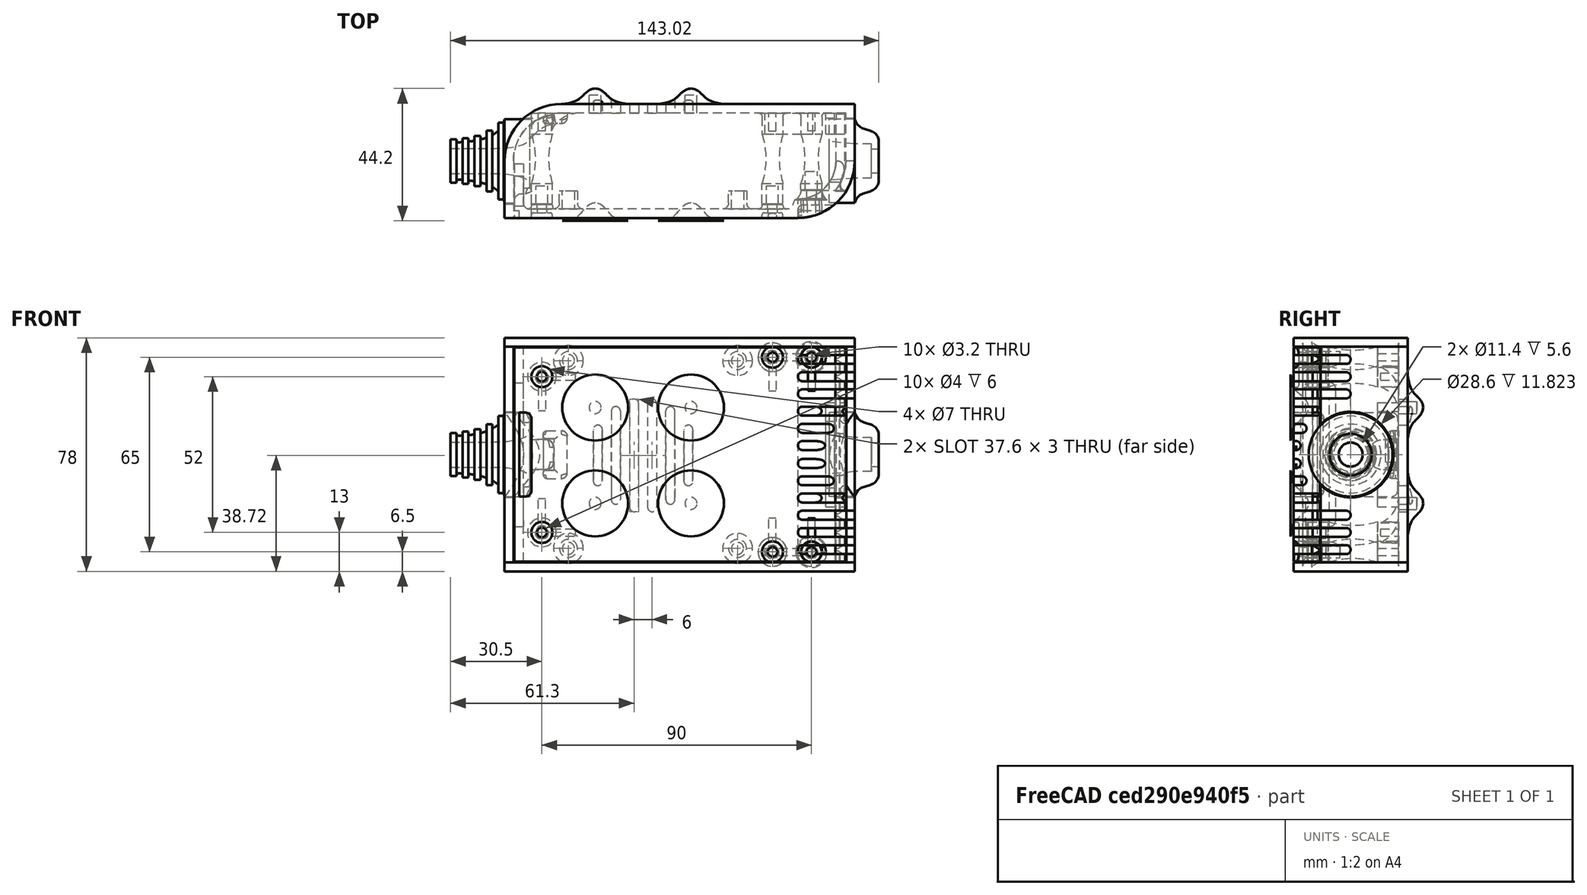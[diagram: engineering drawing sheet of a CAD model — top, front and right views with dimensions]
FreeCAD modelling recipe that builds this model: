
FCSTD DOCUMENT  (FreeCAD 0.19R0.19.2)
Label: enclosure_120
License: All rights reserved
LicenseURL: http://en.wikipedia.org/wiki/All_rights_reserved
objects: Part::Feature×72, Part::Revolution×72, Part::MultiFuse×53, Sketcher::SketchObject×34, Part::Fillet×26, Part::Cut×24, Part::Extrusion×23, Part::Cylinder×22, Part::Box×12, App::MeasureDistance×4
note: 338 computed .brp shape members not serialized (recipe doc carries the construction recipe); baked Part::Feature solids carry a one-line shape summary decoded from their .brp

FEATURE [Sketcher::SketchObject] Sketch  label="topSketch"
  FullyConstrained = true
  sketch-geometry (13):
    g0: LineSegment StartX=117 StartY=19 StartZ=0 EndX=117 EndY=38 EndZ=0
    g1: ArcOfCircle CenterX=98 CenterY=19 CenterZ=0 NormalX=0 NormalY=0 NormalZ=1 AngleXU=0 Radius=19 StartAngle=5.7297 EndAngle=6.28319
    g2: LineSegment StartX=0 StartY=3 StartZ=0 EndX=0 EndY=19 EndZ=0
    g3: LineSegment StartX=19 StartY=38 StartZ=0 EndX=117 EndY=38 EndZ=0
    g4: ArcOfCircle CenterX=19 CenterY=19 CenterZ=0 NormalX=0 NormalY=0 NormalZ=1 AngleXU=0 Radius=19 StartAngle=1.5708 EndAngle=3.14159
    g5: ArcOfCircle CenterX=19 CenterY=19 CenterZ=0 NormalX=0 NormalY=0 NormalZ=1 AngleXU=0 Radius=16 StartAngle=1.5708 EndAngle=3.14159
    g6: ArcOfCircle CenterX=98 CenterY=19 CenterZ=0 NormalX=0 NormalY=0 NormalZ=1 AngleXU=0 Radius=16 StartAngle=5.60905 EndAngle=6.28319
    g7: LineSegment StartX=114 StartY=19 StartZ=0 EndX=114 EndY=35 EndZ=0
    g8: LineSegment StartX=110.5 StartY=9.01251 StartZ=0 EndX=114.163 EndY=9.01251 EndZ=0
    g9: LineSegment StartX=114 StartY=35 StartZ=0 EndX=19 EndY=35 EndZ=0
    g10: LineSegment StartX=0 StartY=3 StartZ=0 EndX=0 EndY=0 EndZ=0
    g11: LineSegment StartX=3 StartY=0 StartZ=0 EndX=0 EndY=0 EndZ=0
    g12: LineSegment StartX=3 StartY=19 StartZ=0 EndX=3 EndY=0 EndZ=0
  constraints (33):
    c: Vertical(g0)
    c: Distance(g0) = 19
    c: Block(g0)
    c: Coincident(g1,g0)
    c: Block(g1)
    c: Vertical(g2)
    c: Block(g2)
    c: Coincident(g3,g0)
    c: Horizontal(g3)
    c: Distance(g3) = 98
    c: Coincident(g4,g3)
    c: Coincident(g4,g2)
    c: Block(g4)
    c: Coincident(g5,g4)
    c: Coincident(g6,g1)
    c: Block(g6)
    c: Block(g5)
    c: Coincident(g7,g6)
    c: Vertical(g7)
    c: Coincident(g8,g6)
    c: Coincident(g8,g1)
    c: Coincident(g9,g7)
    c: Coincident(g9,g5)
    c: Horizontal(g9)
    c: Tangent(g9,g5)
    c: Coincident(g10,g2)
    c: Distance(g10) = 3
    c: Vertical(g10)
    c: Coincident(g11,g10)
    c: Horizontal(g11)
    c: Coincident(g12,g5)
    c: Coincident(g12,g11)
    c: Vertical(g12)
FEATURE [Sketcher::SketchObject] Sketch001  label="bottomSketch"
  FullyConstrained = true
  sketch-geometry (32):
    g0: LineSegment StartX=3.3 StartY=-6.03275e-07 StartZ=0 EndX=98 EndY=-6.03275e-07 EndZ=0
    g1: ArcOfCircle CenterX=98 CenterY=19 CenterZ=0 NormalX=0 NormalY=0 NormalZ=1 AngleXU=0 Radius=19 StartAngle=4.71239 EndAngle=5.71103
    g2: LineSegment StartX=6.3 StartY=8 StartZ=0 EndX=3.3 EndY=8 EndZ=0
    g3: LineSegment StartX=3.3 StartY=8 StartZ=0 EndX=3.3 EndY=-6.03275e-07 EndZ=0
    g4: ArcOfCircle CenterX=8.3 CenterY=5 CenterZ=0 NormalX=0 NormalY=0 NormalZ=1 AngleXU=0 Radius=2 StartAngle=3.14159 EndAngle=4.71239
    g5: LineSegment StartX=6.3 StartY=8 StartZ=0 EndX=6.3 EndY=5 EndZ=0
    g6: ArcOfCircle CenterX=98 CenterY=19 CenterZ=0 NormalX=0 NormalY=0 NormalZ=1 AngleXU=0 Radius=12.7 StartAngle=4.71239 EndAngle=6.28319
    g7: LineSegment StartX=94.7 StartY=3 StartZ=0 EndX=8.3 EndY=3 EndZ=0
    g8-g12: Circle x5 (B-spline internal-alignment scaffolding for g13; pole/knot coordinates omitted)
    g13: BSplineCurve PolesCount=5 KnotsCount=3 Degree=3 IsPeriodic=0
    g14: GeomPoint X=98 Y=6.3 Z=0
    g15: GeomPoint X=96.3938 Y=4.71946 Z=0
    g16: GeomPoint X=94.7 Y=3 Z=0
    g17-g23: Circle x7 (B-spline internal-alignment scaffolding for g24; pole/knot coordinates omitted)
    g24: BSplineCurve PolesCount=7 KnotsCount=5 Degree=3 IsPeriodic=0
    g25-g29: GeomPoint x5 (B-spline internal-alignment scaffolding for g24; pole/knot coordinates omitted)
    g30: ArcOfCircle CenterX=98 CenterY=19 CenterZ=0 NormalX=0 NormalY=0 NormalZ=1 AngleXU=0 Radius=15.7 StartAngle=5.81226 EndAngle=6.28319
    g31: LineSegment StartX=110.7 StartY=19 StartZ=0 EndX=113.7 EndY=19 EndZ=0
  constraints (41):
    c: Horizontal(g0)
    c: Coincident(g1,g0)
    c: Block(g1)
    c: Horizontal(g2)
    c: Distance(g2) = 3
    c: Coincident(g3,g2)
    c: Vertical(g3)
    c: Coincident(g3,g0)
    c: Block(g4)
    c: Block(g2)
    c: Coincident(g5,g2)
    c: Coincident(g5,g4)
    c: Vertical(g5)
    c: Coincident(g6,g1)
    c: Block(g6)
    c: Coincident(g7,g4)
    c: Horizontal(g7)
    c: Block(g0)
    c: Block(g7)
    c: Block(g3)
    c: Coincident(g13,g6)
    c: Weight(g8) = 1
    c: Equal(g8, g9-g12) x4
    c: Coincident(g13,g7)
    c: InternalAlignment(g8-g12 -> g13) x5
    c: InternalAlignment(g14,g13)
    c: InternalAlignment(g15,g13)
    c: InternalAlignment(g16,g13)
    c: Block(g13)
    c: Weight(g17) = 1
    c: Equal(g17, g18-g23) x6
    c: Coincident(g24,g1)
    c: InternalAlignment(g17-g23 -> g24) x7
    c: InternalAlignment(g25-g29 -> g24) x5
    c: Block(g24)
    c: Coincident(g30,g24)
    c: Coincident(g31,g6)
    c: Coincident(g31,g30)
    c: Horizontal(g31)
    c: Block(g31)
    c: Block(g30)
FEATURE [Part::Extrusion] Extrude  label="top"
  Base = -> Sketch
  Dir = (0,0,1)
  DirMode = 2
  FaceMakerClass = Part::FaceMakerBullseye
  LengthFwd = 72
  LengthRev = 0
  Solid = true
  Symmetric = false
FEATURE [Part::Extrusion] Extrude001  label="bottom"
  Base = -> Sketch001
  Dir = (0,0,1)
  DirMode = 2
  FaceMakerClass = Part::FaceMakerBullseye
  LengthFwd = 71.4
  LengthRev = 0
  Placement = pos=(0,0,0.3) rot=(0,0,1;0rad)
  Solid = true
  Symmetric = false
FEATURE [Sketcher::SketchObject] Sketch002  label="topSketch001"
  FullyConstrained = true
  sketch-geometry (6):
    g0: LineSegment StartX=19 StartY=38 StartZ=0 EndX=117 EndY=38 EndZ=0
    g1: ArcOfCircle CenterX=19 CenterY=19 CenterZ=0 NormalX=0 NormalY=0 NormalZ=1 AngleXU=0 Radius=19 StartAngle=1.5708 EndAngle=3.14159
    g2: LineSegment StartX=117 StartY=38 StartZ=0 EndX=117 EndY=19 EndZ=0
    g3: LineSegment StartX=98 StartY=1.0161e-12 StartZ=0 EndX=5.22862e-06 EndY=1.0161e-12 EndZ=0
    g4: LineSegment StartX=5.22862e-06 StartY=19 StartZ=0 EndX=5.22862e-06 EndY=1.0161e-12 EndZ=0
    g5: ArcOfCircle CenterX=98 CenterY=19 CenterZ=0 NormalX=0 NormalY=0 NormalZ=1 AngleXU=0 Radius=19 StartAngle=4.71239 EndAngle=6.28319
  constraints (16):
    c: Horizontal(g0)
    c: Distance(g0) = 98
    c: Coincident(g1,g0)
    c: Block(g1)
    c: Coincident(g2,g0)
    c: Vertical(g2)
    c: Distance(g2) = 19
    c: Horizontal(g3)
    c: Coincident(g4,g1)
    c: Vertical(g4)
    c: Coincident(g3,g4)
    c: Block(g3)
    c: Coincident(g5,g2)
    c: Coincident(g5,g3)
    c: Block(g0)
    c: Block(g5)
FEATURE [Part::Extrusion] Extrude002  label="sideA"
  Base = -> Sketch002
  Dir = (0,0,1)
  DirMode = 2
  FaceMakerClass = Part::FaceMakerBullseye
  LengthFwd = 3
  LengthRev = 0
  Placement = pos=(0,0,-3) rot=(0,0,1;0rad)
  Solid = true
  Symmetric = false
FEATURE [Sketcher::SketchObject] Sketch003  label="topSketch002"
  FullyConstrained = true
  sketch-geometry (6):
    g0: LineSegment StartX=19 StartY=38 StartZ=0 EndX=117 EndY=38 EndZ=0
    g1: ArcOfCircle CenterX=19 CenterY=19 CenterZ=0 NormalX=0 NormalY=0 NormalZ=1 AngleXU=0 Radius=19 StartAngle=1.5708 EndAngle=3.14159
    g2: LineSegment StartX=117 StartY=38 StartZ=0 EndX=117 EndY=19 EndZ=0
    g3: LineSegment StartX=98 StartY=1.0161e-12 StartZ=0 EndX=5.22862e-06 EndY=1.0161e-12 EndZ=0
    g4: LineSegment StartX=5.22862e-06 StartY=19 StartZ=0 EndX=5.22862e-06 EndY=1.0161e-12 EndZ=0
    g5: ArcOfCircle CenterX=98 CenterY=19 CenterZ=0 NormalX=0 NormalY=0 NormalZ=1 AngleXU=0 Radius=19 StartAngle=4.71239 EndAngle=6.28319
  constraints (16):
    c: Horizontal(g0)
    c: Distance(g0) = 98
    c: Coincident(g1,g0)
    c: Block(g1)
    c: Coincident(g2,g0)
    c: Vertical(g2)
    c: Distance(g2) = 19
    c: Horizontal(g3)
    c: Coincident(g4,g1)
    c: Vertical(g4)
    c: Coincident(g3,g4)
    c: Block(g3)
    c: Coincident(g5,g2)
    c: Coincident(g5,g3)
    c: Block(g0)
    c: Block(g5)
FEATURE [Part::Extrusion] Extrude003  label="sideB"
  Base = -> Sketch003
  Dir = (0,0,1)
  DirMode = 2
  FaceMakerClass = Part::FaceMakerBullseye
  LengthFwd = 3
  LengthRev = 0
  Placement = pos=(0,0,72) rot=(0,0,1;0rad)
  Solid = true
  Symmetric = false
FEATURE [Sketcher::SketchObject] Sketch004
  FullyConstrained = true
  MapMode = 3
  Placement = pos=(0,0,0) rot=(1,0,0;1.5708rad)
  Support = -> [Extrude]
  sketch-geometry (8):
    g0: Circle CenterX=80.351 CenterY=-67.6202 CenterZ=0 NormalX=0 NormalY=0 NormalZ=1 AngleXU=0 Radius=2
    g1: Circle CenterX=80.351 CenterY=-67.6202 CenterZ=0 NormalX=0 NormalY=0 NormalZ=1 AngleXU=0 Radius=3
    g2: Circle CenterX=80.351 CenterY=-4.92017 CenterZ=0 NormalX=0 NormalY=0 NormalZ=1 AngleXU=0 Radius=2
    g3: Circle CenterX=80.351 CenterY=-4.92017 CenterZ=0 NormalX=0 NormalY=0 NormalZ=1 AngleXU=0 Radius=3
    g4: Circle CenterX=23.851 CenterY=-4.92017 CenterZ=0 NormalX=0 NormalY=0 NormalZ=1 AngleXU=0 Radius=2
    g5: Circle CenterX=23.851 CenterY=-4.92017 CenterZ=0 NormalX=0 NormalY=0 NormalZ=1 AngleXU=0 Radius=3
    g6: Circle CenterX=23.851 CenterY=-67.6202 CenterZ=0 NormalX=0 NormalY=0 NormalZ=1 AngleXU=0 Radius=2
    g7: Circle CenterX=23.851 CenterY=-67.6202 CenterZ=0 NormalX=0 NormalY=0 NormalZ=1 AngleXU=0 Radius=3
  constraints (8):
    c: Block(g3)
    c: Block(g2)
    c: Block(g1)
    c: Block(g0)
    c: Block(g6)
    c: Block(g7)
    c: Block(g4)
    c: Block(g5)
FEATURE [Part::Extrusion] Extrude004
  Base = -> Sketch004
  Dir = (0,-1,2e-16)
  DirMode = 2
  FaceMakerClass = Part::FaceMakerBullseye
  LengthFwd = 6
  LengthRev = 0
  Placement = pos=(0,9,0) rot=(0,0,1;0rad)
  Solid = true
  Symmetric = false
FEATURE [Sketcher::SketchObject] Sketch005
  FullyConstrained = true
  MapMode = 3
  Placement = pos=(0,0,0) rot=(1,0,0;1.5708rad)
  Support = -> [Extrude]
  sketch-geometry (8):
    g0: Circle CenterX=80.351 CenterY=-67.6202 CenterZ=0 NormalX=0 NormalY=0 NormalZ=1 AngleXU=0 Radius=3
    g1: Circle CenterX=80.351 CenterY=-4.92017 CenterZ=0 NormalX=0 NormalY=0 NormalZ=1 AngleXU=0 Radius=3
    g2: Circle CenterX=23.851 CenterY=-4.92017 CenterZ=0 NormalX=0 NormalY=0 NormalZ=1 AngleXU=0 Radius=3
    g3: Circle CenterX=23.851 CenterY=-67.6202 CenterZ=0 NormalX=0 NormalY=0 NormalZ=1 AngleXU=0 Radius=3
    g4: Circle CenterX=23.851 CenterY=-67.6202 CenterZ=0 NormalX=0 NormalY=0 NormalZ=1 AngleXU=0 Radius=5
    g5: Circle CenterX=80.351 CenterY=-67.6202 CenterZ=0 NormalX=0 NormalY=0 NormalZ=1 AngleXU=0 Radius=5
    g6: Circle CenterX=23.851 CenterY=-4.92017 CenterZ=0 NormalX=0 NormalY=0 NormalZ=1 AngleXU=0 Radius=5
    g7: Circle CenterX=80.351 CenterY=-4.92017 CenterZ=0 NormalX=0 NormalY=0 NormalZ=1 AngleXU=0 Radius=5
  constraints (8):
    c: Block(g1)
    c: Block(g0)
    c: Block(g3)
    c: Block(g2)
    c: Block(g5)
    c: Block(g4)
    c: Block(g6)
    c: Block(g7)
FEATURE [Part::Extrusion] Extrude005
  Base = -> Sketch005
  Dir = (0,-1,2e-16)
  DirMode = 2
  FaceMakerClass = Part::FaceMakerBullseye
  LengthFwd = 2
  LengthRev = 0
  Solid = true
  Symmetric = false
FEATURE [Sketcher::SketchObject] Sketch006
  FullyConstrained = true
  MapMode = 3
  Placement = pos=(0,0,0) rot=(1,0,0;1.5708rad)
  sketch-geometry (8):
    g0: Circle CenterX=80.351 CenterY=-67.6202 CenterZ=0 NormalX=0 NormalY=0 NormalZ=1 AngleXU=0 Radius=3
    g1: Circle CenterX=80.351 CenterY=-4.92017 CenterZ=0 NormalX=0 NormalY=0 NormalZ=1 AngleXU=0 Radius=3
    g2: Circle CenterX=23.851 CenterY=-4.92017 CenterZ=0 NormalX=0 NormalY=0 NormalZ=1 AngleXU=0 Radius=3
    g3: Circle CenterX=23.851 CenterY=-67.6202 CenterZ=0 NormalX=0 NormalY=0 NormalZ=1 AngleXU=0 Radius=3
    g4: Circle CenterX=23.851 CenterY=-67.6202 CenterZ=0 NormalX=0 NormalY=0 NormalZ=1 AngleXU=0 Radius=5
    g5: Circle CenterX=80.351 CenterY=-67.6202 CenterZ=0 NormalX=0 NormalY=0 NormalZ=1 AngleXU=0 Radius=5
    g6: Circle CenterX=23.851 CenterY=-4.92017 CenterZ=0 NormalX=0 NormalY=0 NormalZ=1 AngleXU=0 Radius=5
    g7: Circle CenterX=80.351 CenterY=-4.92017 CenterZ=0 NormalX=0 NormalY=0 NormalZ=1 AngleXU=0 Radius=5
  constraints (8):
    c: Block(g1)
    c: Block(g0)
    c: Block(g3)
    c: Block(g2)
    c: Block(g5)
    c: Block(g4)
    c: Block(g6)
    c: Block(g7)
FEATURE [Part::Extrusion] Extrude007
  Base = -> Sketch006
  Dir = (0,-1,2e-16)
  DirMode = 2
  FaceMakerClass = Part::FaceMakerBullseye
  LengthFwd = 2
  LengthRev = 0
  Solid = true
  Symmetric = false
FEATURE [Part::Fillet] Fillet
  Base = -> Extrude007
  Edges = 4 edges r=1.99: [Edge6,Edge12,Edge18,Edge24]
FEATURE [Part::Cut] Cut
  Base = -> Extrude005
  Placement = pos=(0,5,0) rot=(0,0,1;0rad)
  Tool = -> Fillet
FEATURE [Part::MultiFuse] Fusion  label="pCBScrews"
  Placement = pos=(-2.5,0,72.3) rot=(0,0,1;0rad)
  Shapes = -> [Extrude004,Cut]
FEATURE [App::MeasureDistance] Distance  label="Distance: 0.69 mm"
  Distance = 0.685967
  P1 = (24.0138,2.9647,0.3)
  P2 = (23.8901,3,-0.373787)
FEATURE [App::MeasureDistance] Distance001  label="Distance: 0.53 mm"
  Distance = 0.533607
  P1 = (80.2939,3,72.2334)
  P2 = (80.281,2.99661,71.7)
FEATURE [Part::Fillet] Fillet001
  Base = -> Extrude001
  Edges = 1 edges r=2.4: [Edge17]
FEATURE [Part::Fillet] Fillet002  label="bottom001"
  Base = -> Fillet001
  Edges = 1 edges r=2.4: [Edge36]
FEATURE [Part::Fillet] Fillet003  label="top001"
  Base = -> Extrude
  Edges = 1 edges r=2: [Edge1]
FEATURE [Sketcher::SketchObject] Sketch007
  FullyConstrained = true
  sketch-geometry (16):
    g0: LineSegment StartX=4 StartY=0 StartZ=0 EndX=4 EndY=2.4 EndZ=0
    g1: LineSegment StartX=4 StartY=2.4 StartZ=0 EndX=7 EndY=2.4 EndZ=0
    g2: LineSegment StartX=4 StartY=0 StartZ=0 EndX=5.7 EndY=0 EndZ=0
    g3: LineSegment StartX=5.7 StartY=0 StartZ=0 EndX=5.7 EndY=-5.6 EndZ=0
    g4-g8: Circle x5 (B-spline internal-alignment scaffolding for g9; pole/knot coordinates omitted)
    g9: BSplineCurve PolesCount=5 KnotsCount=3 Degree=3 IsPeriodic=0
    g10: GeomPoint X=7 Y=2.4 Z=0
    g11: GeomPoint X=10.4582 Y=-1.55472 Z=0
    g12: GeomPoint X=14 Y=-5.6 Z=0
    g13: LineSegment StartX=14 StartY=-5.6 StartZ=0 EndX=14 EndY=-14.1 EndZ=0
    g14: LineSegment StartX=14 StartY=-14.1 StartZ=0 EndX=6.5 EndY=-14.1 EndZ=0
    g15: LineSegment StartX=5.7 StartY=-5.6 StartZ=0 EndX=6.5 EndY=-14.1 EndZ=0
  constraints (28):
    c: Distance(g0) = 2.4
    c: Vertical(g0)
    c: Block(g0)
    c: Coincident(g1,g0)
    c: Horizontal(g1)
    c: Distance(g1) = 3
    c: Coincident(g2,g0)
    c: Horizontal(g2)
    c: Distance(g2) = 1.7
    c: Coincident(g3,g2)
    c: Vertical(g3)
    c: Distance(g3) = 5.6
    c: Coincident(g9,g1)
    c: Weight(g4) = 1
    c: Equal(g4, g5-g8) x4
    c: InternalAlignment(g4-g8 -> g9) x5
    c: InternalAlignment(g10,g9)
    c: InternalAlignment(g11,g9)
    c: InternalAlignment(g12,g9)
    c: Block(g9)
    c: Coincident(g13,g9)
    c: Vertical(g13)
    c: Distance(g13) = 8.5
    c: Coincident(g14,g13)
    c: Horizontal(g14)
    c: Distance(g14) = 7.5
    c: Coincident(g15,g3)
    c: Coincident(g15,g14)
FEATURE [Part::Feature] Face
  shape: bbox 10 x 16.5 x 2e-07 mm, 1 faces, 0 solids (baked)
FEATURE [Part::Revolution] Revolve  label="plugHousing"
  Angle = 360
  Axis = (0,1,0)
  Base = (0,0,0)
  FaceMakerClass = Part::FaceMakerBullseye
  Placement = pos=(0,0,36.15) rot=(0,0,1;0rad)
  Solid = false
  Source = -> Face
  Symmetric = false
FEATURE [Part::Feature] Face001
  shape: bbox 10 x 16.5 x 2e-07 mm, 1 faces, 0 solids (baked)
FEATURE [Part::Revolution] Revolve001  label="plugHousing001"
  Angle = 360
  Axis = (0,1,0)
  Base = (0,0,0)
  FaceMakerClass = Part::FaceMakerBullseye
  Placement = pos=(0,0,36.15) rot=(0,0,1;0rad)
  Solid = false
  Source = -> Face001
  Symmetric = false
FEATURE [Part::MultiFuse] Fusion001  label="plugHousing002"
  Placement = pos=(0,0,0) rot=(0,0,1;1.5708rad)
  Shapes = -> [Revolve001,Revolve]
FEATURE [Part::Feature] Face002
  shape: bbox 10 x 16.5 x 2e-07 mm, 1 faces, 0 solids (baked)
FEATURE [Part::Revolution] Revolve003  label="plugHousing005"
  Angle = 360
  Axis = (0,1,0)
  Base = (0,0,0)
  FaceMakerClass = Part::FaceMakerBullseye
  Placement = pos=(0,0,36.15) rot=(0,0,1;0rad)
  Solid = false
  Source = -> Face002
  Symmetric = false
FEATURE [Part::Feature] Face003
  shape: bbox 10 x 16.5 x 2e-07 mm, 1 faces, 0 solids (baked)
FEATURE [Part::Revolution] Revolve002  label="plugHousing003"
  Angle = 360
  Axis = (0,1,0)
  Base = (0,0,0)
  FaceMakerClass = Part::FaceMakerBullseye
  Placement = pos=(0,0,36.15) rot=(0,0,1;0rad)
  Solid = false
  Source = -> Face003
  Symmetric = false
FEATURE [Part::MultiFuse] Fusion002  label="plugHousing004"
  Placement = pos=(0,0,0) rot=(0,0,1;1.5708rad)
  Shapes = -> [Revolve002,Revolve003]
FEATURE [Part::MultiFuse] Fusion003  label="plugHousing006"
  Placement = pos=(0,19,0) rot=(0,0,1;3.14159rad)
  Shapes = -> [Fusion002,Fusion001]
FEATURE [Part::Feature] Face004
  shape: bbox 10 x 16.5 x 2e-07 mm, 1 faces, 0 solids (baked)
FEATURE [Part::Revolution] Revolve006  label="plugHousing010"
  Angle = 360
  Axis = (0,1,0)
  Base = (0,0,0)
  FaceMakerClass = Part::FaceMakerBullseye
  Placement = pos=(0,0,36.15) rot=(0,0,1;0rad)
  Solid = false
  Source = -> Face004
  Symmetric = false
FEATURE [Part::Feature] Face005
  shape: bbox 10 x 16.5 x 2e-07 mm, 1 faces, 0 solids (baked)
FEATURE [Part::Revolution] Revolve007  label="plugHousing011"
  Angle = 360
  Axis = (0,1,0)
  Base = (0,0,0)
  FaceMakerClass = Part::FaceMakerBullseye
  Placement = pos=(0,0,36.15) rot=(0,0,1;0rad)
  Solid = false
  Source = -> Face005
  Symmetric = false
FEATURE [Part::Feature] Face006
  shape: bbox 10 x 16.5 x 2e-07 mm, 1 faces, 0 solids (baked)
FEATURE [Part::Revolution] Revolve004  label="plugHousing007"
  Angle = 360
  Axis = (0,1,0)
  Base = (0,0,0)
  FaceMakerClass = Part::FaceMakerBullseye
  Placement = pos=(0,0,36.15) rot=(0,0,1;0rad)
  Solid = false
  Source = -> Face006
  Symmetric = false
FEATURE [Part::MultiFuse] Fusion004  label="plugHousing009"
  Placement = pos=(0,0,0) rot=(0,0,1;1.5708rad)
  Shapes = -> [Revolve004,Revolve007]
FEATURE [Part::Feature] Face007
  shape: bbox 10 x 16.5 x 2e-07 mm, 1 faces, 0 solids (baked)
FEATURE [Part::Revolution] Revolve005  label="plugHousing008"
  Angle = 360
  Axis = (0,1,0)
  Base = (0,0,0)
  FaceMakerClass = Part::FaceMakerBullseye
  Placement = pos=(0,0,36.15) rot=(0,0,1;0rad)
  Solid = false
  Source = -> Face007
  Symmetric = false
FEATURE [Part::MultiFuse] Fusion005  label="plugHousing012"
  Placement = pos=(0,0,0) rot=(0,0,1;1.5708rad)
  Shapes = -> [Revolve006,Revolve005]
FEATURE [Part::MultiFuse] Fusion006  label="plugHousing013"
  Placement = pos=(0,19,0) rot=(0,0,1;3.14159rad)
  Shapes = -> [Fusion005,Fusion004]
FEATURE [Part::MultiFuse] Fusion007  label="plugHousing014"
  Placement = pos=(122.621,0,-0.15) rot=(0,0,1;0rad)
  Shapes = -> [Fusion003,Fusion006]
FEATURE [Part::Cylinder] Cylinder002
  Angle = 360
  AttacherType = Attacher::AttachEngine3D
  Height = 20
  Placement = pos=(0,0,36.15) rot=(0,0,1;0rad)
  Radius = 4
FEATURE [Part::Cylinder] Cylinder003
  Angle = 360
  AttacherType = Attacher::AttachEngine3D
  Height = 10
  Placement = pos=(0,0,36.15) rot=(0,0,1;0rad)
  Radius = 4
FEATURE [Part::MultiFuse] Fusion009  label="removeToCreateHoleForPlugHousing"
  Placement = pos=(70,19,36.15) rot=(0,1,0;1.5708rad)
  Shapes = -> [Cylinder002,Cylinder003]
FEATURE [Part::Cylinder] Cylinder004
  Angle = 360
  AttacherType = Attacher::AttachEngine3D
  Height = 20
  Placement = pos=(0,0,36.15) rot=(0,0,1;0rad)
  Radius = 4
FEATURE [Part::Cylinder] Cylinder005
  Angle = 360
  AttacherType = Attacher::AttachEngine3D
  Height = 10
  Placement = pos=(0,0,36.15) rot=(0,0,1;0rad)
  Radius = 4
FEATURE [Part::MultiFuse] Fusion010  label="removeToCreateHoleForPlugHousing001"
  Placement = pos=(70,19,36.15) rot=(0,1,0;1.5708rad)
  Shapes = -> [Cylinder004,Cylinder005]
FEATURE [Part::Cut] Cut001
  Base = -> Fillet003
  Tool = -> Fusion010
FEATURE [Part::Cut] Cut002  label="Bottom"
  Base = -> Fillet002
  Tool = -> Fusion009
FEATURE [Part::Feature] Face008
  shape: bbox 10 x 16.5 x 2e-07 mm, 1 faces, 0 solids (baked)
FEATURE [Part::Revolution] Revolve011  label="plugHousing021"
  Angle = 360
  Axis = (0,1,0)
  Base = (0,0,0)
  FaceMakerClass = Part::FaceMakerBullseye
  Placement = pos=(0,0,36.15) rot=(0,0,1;0rad)
  Solid = false
  Source = -> Face008
  Symmetric = false
FEATURE [Part::Feature] Face009
  shape: bbox 10 x 16.5 x 2e-07 mm, 1 faces, 0 solids (baked)
FEATURE [Part::Revolution] Revolve012  label="plugHousing022"
  Angle = 360
  Axis = (0,1,0)
  Base = (0,0,0)
  FaceMakerClass = Part::FaceMakerBullseye
  Placement = pos=(0,0,36.15) rot=(0,0,1;0rad)
  Solid = false
  Source = -> Face009
  Symmetric = false
FEATURE [Part::Feature] Face010 .. Face013  x4 (patterned run collapsed; names and placements below)
  shape: bbox 10 x 16.5 x 2e-07 mm, 1 faces, 0 solids (baked)
FEATURE [Part::Revolution] Revolve015  label="plugHousing027"
  Angle = 360
  Axis = (0,1,0)
  Base = (0,0,0)
  FaceMakerClass = Part::FaceMakerBullseye
  Placement = pos=(0,0,36.15) rot=(0,0,1;0rad)
  Solid = false
  Source = -> Face013
  Symmetric = false
FEATURE [Part::Feature] Face014
  shape: bbox 10 x 16.5 x 2e-07 mm, 1 faces, 0 solids (baked)
FEATURE [Part::Feature] Face015
  shape: bbox 10 x 16.5 x 2e-07 mm, 1 faces, 0 solids (baked)
FEATURE [Part::Feature] Face016
  shape: bbox 10 x 16.5 x 2e-07 mm, 1 faces, 0 solids (baked)
FEATURE [Part::Revolution] Revolve019  label="plugHousing033"
  Angle = 360
  Axis = (0,1,0)
  Base = (0,0,0)
  FaceMakerClass = Part::FaceMakerBullseye
  Placement = pos=(0,0,36.15) rot=(0,0,1;0rad)
  Solid = false
  Source = -> Face016
  Symmetric = false
FEATURE [Part::Feature] Face017
  shape: bbox 10 x 16.5 x 2e-07 mm, 1 faces, 0 solids (baked)
FEATURE [Part::Revolution] Revolve020  label="plugHousing034"
  Angle = 360
  Axis = (0,1,0)
  Base = (0,0,0)
  FaceMakerClass = Part::FaceMakerBullseye
  Placement = pos=(0,0,36.15) rot=(0,0,1;0rad)
  Solid = false
  Source = -> Face017
  Symmetric = false
FEATURE [Part::Feature] Face018
  shape: bbox 10 x 16.5 x 2e-07 mm, 1 faces, 0 solids (baked)
FEATURE [Part::Revolution] Revolve016  label="plugHousing030"
  Angle = 360
  Axis = (0,1,0)
  Base = (0,0,0)
  FaceMakerClass = Part::FaceMakerBullseye
  Placement = pos=(0,0,36.15) rot=(0,0,1;0rad)
  Solid = false
  Source = -> Face018
  Symmetric = false
FEATURE [Part::MultiFuse] Fusion020  label="plugHousing038"
  Placement = pos=(0,0,0) rot=(0,0,1;1.5708rad)
  Shapes = -> [Revolve016,Revolve020]
FEATURE [Part::Feature] Face019
  shape: bbox 10 x 16.5 x 2e-07 mm, 1 faces, 0 solids (baked)
FEATURE [Part::Feature] Face020
  shape: bbox 10 x 16.5 x 2e-07 mm, 1 faces, 0 solids (baked)
FEATURE [Part::Revolution] Revolve017  label="plugHousing031"
  Angle = 360
  Axis = (0,1,0)
  Base = (0,0,0)
  FaceMakerClass = Part::FaceMakerBullseye
  Placement = pos=(0,0,36.15) rot=(0,0,1;0rad)
  Solid = false
  Source = -> Face020
  Symmetric = false
FEATURE [Part::MultiFuse] Fusion021  label="plugHousing039"
  Placement = pos=(0,0,0) rot=(0,0,1;1.5708rad)
  Shapes = -> [Revolve019,Revolve017]
FEATURE [Part::MultiFuse] Fusion023  label="plugHousing041"
  Placement = pos=(0,19,0) rot=(0,0,1;3.14159rad)
  Shapes = -> [Fusion021,Fusion020]
FEATURE [Part::Revolution] Revolve022  label="plugHousing043"
  Angle = 360
  Axis = (0,1,0)
  Base = (0,0,0)
  FaceMakerClass = Part::FaceMakerBullseye
  Placement = pos=(0,0,36.15) rot=(0,0,1;0rad)
  Solid = false
  Source = -> Face019
  Symmetric = false
FEATURE [Part::Feature] Face021
  shape: bbox 10 x 16.5 x 2e-07 mm, 1 faces, 0 solids (baked)
FEATURE [Part::Revolution] Revolve023  label="plugHousing044"
  Angle = 360
  Axis = (0,1,0)
  Base = (0,0,0)
  FaceMakerClass = Part::FaceMakerBullseye
  Placement = pos=(0,0,36.15) rot=(0,0,1;0rad)
  Solid = false
  Source = -> Face021
  Symmetric = false
FEATURE [Part::Feature] Face022
  shape: bbox 10 x 16.5 x 2e-07 mm, 1 faces, 0 solids (baked)
FEATURE [Part::Revolution] Revolve018  label="plugHousing032"
  Angle = 360
  Axis = (0,1,0)
  Base = (0,0,0)
  FaceMakerClass = Part::FaceMakerBullseye
  Placement = pos=(0,0,36.15) rot=(0,0,1;0rad)
  Solid = false
  Source = -> Face022
  Symmetric = false
FEATURE [Part::MultiFuse] Fusion022  label="plugHousing040"
  Placement = pos=(0,0,0) rot=(0,0,1;1.5708rad)
  Shapes = -> [Revolve018,Revolve023]
FEATURE [Part::Feature] Face023
  shape: bbox 10 x 16.5 x 2e-07 mm, 1 faces, 0 solids (baked)
FEATURE [Part::Revolution] Revolve021  label="plugHousing035"
  Angle = 360
  Axis = (0,1,0)
  Base = (0,0,0)
  FaceMakerClass = Part::FaceMakerBullseye
  Placement = pos=(0,0,36.15) rot=(0,0,1;0rad)
  Solid = false
  Source = -> Face023
  Symmetric = false
FEATURE [Part::MultiFuse] Fusion018  label="plugHousing036"
  Placement = pos=(0,0,0) rot=(0,0,1;1.5708rad)
  Shapes = -> [Revolve022,Revolve021]
FEATURE [Part::MultiFuse] Fusion019  label="plugHousing037"
  Placement = pos=(0,19,0) rot=(0,0,1;3.14159rad)
  Shapes = -> [Fusion018,Fusion022]
FEATURE [Part::MultiFuse] Fusion024  label="plugHousing042"
  Placement = pos=(122.621,0,-0.15) rot=(0,0,1;0rad)
  Shapes = -> [Fusion023,Fusion019]
FEATURE [Part::Cylinder] Cylinder006
  Angle = 360
  AttacherType = Attacher::AttachEngine3D
  Height = 20
  Placement = pos=(0,0,36.15) rot=(0,0,1;0rad)
  Radius = 14.3
FEATURE [Part::Cylinder] Cylinder007
  Angle = 360
  AttacherType = Attacher::AttachEngine3D
  Height = 10
  Placement = pos=(0,0,36.15) rot=(0,0,1;0rad)
  Radius = 4
FEATURE [Part::MultiFuse] Fusion026  label="removeToCreteHoleForPlugHousing"
  Placement = pos=(70,19,36) rot=(0,1,0;1.5708rad)
  Shapes = -> [Cylinder006,Cylinder007]
FEATURE [Part::Box] Box001  label="Cube001"
  AttacherType = Attacher::AttachEngine3D
  Height = 28
  Length = 3
  Placement = pos=(110.7,19,22) rot=(0,0,1;0rad)
  Width = 15.7
FEATURE [Part::Cut] Cut003  label="top002"
  Base = -> Cut001
  Tool = -> Fusion007
FEATURE [Part::Revolution] Revolve008  label="plugHousing015"
  Angle = 360
  Axis = (0,1,0)
  Base = (0,0,0)
  FaceMakerClass = Part::FaceMakerBullseye
  Placement = pos=(0,0,36.15) rot=(0,0,1;0rad)
  Solid = false
  Source = -> Face010
  Symmetric = false
FEATURE [Part::MultiFuse] Fusion013  label="plugHousing020"
  Placement = pos=(0,0,0) rot=(0,0,1;1.5708rad)
  Shapes = -> [Revolve008,Revolve012]
FEATURE [Part::Cut] Cut004  label="top003"
  Base = -> Cut003
  Placement = pos=(1,0,0) rot=(0,0,1;0rad)
  Tool = -> Fusion026
FEATURE [Part::Cylinder] Cylinder008
  Angle = 360
  AttacherType = Attacher::AttachEngine3D
  Height = 20
  Placement = pos=(0,0,36.15) rot=(0,0,1;0rad)
  Radius = 10.3
FEATURE [Part::Cylinder] Cylinder009
  Angle = 360
  AttacherType = Attacher::AttachEngine3D
  Height = 10
  Placement = pos=(0,0,36.15) rot=(0,0,1;0rad)
  Radius = 4
FEATURE [Part::MultiFuse] Fusion027  label="removeToCreteHoleForPlugHousing001"
  Placement = pos=(70,19,36) rot=(0,1,0;1.5708rad)
  Shapes = -> [Cylinder008,Cylinder009]
FEATURE [Part::Cut] Cut005  label="plugHousingTab"
  Base = -> Box001
  Tool = -> Fusion027
FEATURE [Part::MultiFuse] Fusion028  label="plugHousing045"
  Shapes = -> [Fusion024,Cut005]
FEATURE [Part::Box] Box002  label="Cube002"
  AttacherType = Attacher::AttachEngine3D
  Height = 28.8
  Length = 3
  Placement = pos=(107.3,28,21.6) rot=(0,0,1;0rad)
  Width = 7
FEATURE [Part::Box] Box003  label="Cube003"
  AttacherType = Attacher::AttachEngine3D
  Height = 3
  Length = 6.4
  Placement = pos=(107.3,28,18.6) rot=(0,0,1;0rad)
  Width = 7
FEATURE [Part::Box] Box004  label="Cube004"
  AttacherType = Attacher::AttachEngine3D
  Height = 3
  Length = 6.4
  Placement = pos=(107.3,28,50.4) rot=(0,0,1;0rad)
  Width = 7
FEATURE [Part::MultiFuse] Fusion029  label="plugHousingBracketHolder"
  Shapes = -> [Box004,Box002,Box003]
FEATURE [Part::Cylinder] Cylinder010
  Angle = 360
  AttacherType = Attacher::AttachEngine3D
  Height = 20
  Placement = pos=(0,0,36.15) rot=(0,0,1;0rad)
  Radius = 14.3
FEATURE [Part::Cylinder] Cylinder011
  Angle = 360
  AttacherType = Attacher::AttachEngine3D
  Height = 10
  Placement = pos=(0,0,36.15) rot=(0,0,1;0rad)
  Radius = 4
FEATURE [Part::MultiFuse] Fusion030  label="removeToCreteHoleForPlugHousing002"
  Placement = pos=(70,19,36) rot=(0,1,0;1.5708rad)
  Shapes = -> [Cylinder010,Cylinder011]
FEATURE [Part::Cut] Cut006  label="plugHousingBracketHolder001"
  Base = -> Fusion029
  Tool = -> Fusion030
FEATURE [Part::Cylinder] Cylinder012
  Angle = 360
  AttacherType = Attacher::AttachEngine3D
  Height = 20
  Placement = pos=(0,0,36.15) rot=(0,0,1;0rad)
  Radius = 7
FEATURE [Part::Cylinder] Cylinder013
  Angle = 360
  AttacherType = Attacher::AttachEngine3D
  Height = 10
  Placement = pos=(0,0,36.15) rot=(0,0,1;0rad)
  Radius = 4
FEATURE [Part::MultiFuse] Fusion032  label="removeToCreteHoleForPlugHousing003"
  Placement = pos=(70,19,36) rot=(0,1,0;1.5708rad)
  Shapes = -> [Cylinder012,Cylinder013]
FEATURE [Part::Cut] Cut007  label="bottom002"
  Base = -> Cut002
  Tool = -> Fusion032
FEATURE [Sketcher::SketchObject] Sketch008
  FullyConstrained = true
  sketch-geometry (54):
    g0: LineSegment StartX=-4.2 StartY=0 StartZ=0 EndX=-6.2 EndY=0 EndZ=0
    g1: LineSegment StartX=-14 StartY=-18 StartZ=0 EndX=-14 EndY=-26.5 EndZ=0
    g2: LineSegment StartX=-4.2 StartY=0 StartZ=0 EndX=-4.2 EndY=-13.4877 EndZ=0
    g3: Circle CenterX=-4.2 CenterY=-13.4877 CenterZ=0 NormalX=0 NormalY=0 NormalZ=1 AngleXU=0 Radius=1
    g4: Circle CenterX=-4.2 CenterY=-26.5 CenterZ=0 NormalX=0 NormalY=0 NormalZ=1 AngleXU=0 Radius=1
    g5: Circle CenterX=-8.2 CenterY=-26.5 CenterZ=0 NormalX=0 NormalY=0 NormalZ=1 AngleXU=0 Radius=1
    g6: BSplineCurve PolesCount=3 KnotsCount=2 Degree=2 IsPeriodic=0
    g7: GeomPoint X=-4.2 Y=-13.4877 Z=0
    g8: GeomPoint X=-8.2 Y=-26.5 Z=0
    g9: LineSegment StartX=-14 StartY=-26.5 StartZ=0 EndX=-8.2 EndY=-26.5 EndZ=0
    g10: LineSegment StartX=-10.15 StartY=-12 StartZ=0 EndX=-10.15 EndY=-14 EndZ=0
    g11: LineSegment StartX=-12.8401 StartY=-16 StartZ=0 EndX=-10.1571 EndY=-16 EndZ=0
    g12: LineSegment StartX=-10.15 StartY=-14 StartZ=0 EndX=-8.70761 EndY=-14 EndZ=0
    g13: LineSegment StartX=-12.8401 StartY=-16 StartZ=0 EndX=-12.8401 EndY=-17.6958 EndZ=0
    g14: LineSegment StartX=-10.15 StartY=-12 StartZ=0 EndX=-7.79258 EndY=-12 EndZ=0
    g15: Circle CenterX=-6.2215 CenterY=-2 CenterZ=0 NormalX=0 NormalY=0 NormalZ=1 AngleXU=0 Radius=1
    g16: Circle CenterX=-6.22762 CenterY=-2.58724 CenterZ=0 NormalX=0 NormalY=0 NormalZ=1 AngleXU=0 Radius=1
    g17: Circle CenterX=-6.32538 CenterY=-4 CenterZ=0 NormalX=0 NormalY=0 NormalZ=1 AngleXU=0 Radius=1
    g18: BSplineCurve PolesCount=3 KnotsCount=2 Degree=2 IsPeriodic=0
    g19: GeomPoint X=-6.2215 Y=-2 Z=0
    g20: GeomPoint X=-6.32538 Y=-4 Z=0
    g21: Circle CenterX=-6.48644 CenterY=-5.99526 CenterZ=0 NormalX=0 NormalY=0 NormalZ=1 AngleXU=0 Radius=1
    g22: Circle CenterX=-6.58486 CenterY=-6.99526 CenterZ=0 NormalX=0 NormalY=0 NormalZ=1 AngleXU=0 Radius=1
    g23: Circle CenterX=-6.77343 CenterY=-8 CenterZ=0 NormalX=0 NormalY=0 NormalZ=1 AngleXU=0 Radius=1
    g24: BSplineCurve PolesCount=3 KnotsCount=2 Degree=2 IsPeriodic=0
    g25: GeomPoint X=-6.48644 Y=-5.99526 Z=0
    g26: GeomPoint X=-6.77343 Y=-8 Z=0
    g27: Circle CenterX=-7.19003 CenterY=-10 CenterZ=0 NormalX=0 NormalY=0 NormalZ=1 AngleXU=0 Radius=1
    g28: Circle CenterX=-7.44407 CenterY=-11.0915 CenterZ=0 NormalX=0 NormalY=0 NormalZ=1 AngleXU=0 Radius=1
    g29: Circle CenterX=-7.79258 CenterY=-12 CenterZ=0 NormalX=0 NormalY=0 NormalZ=1 AngleXU=0 Radius=1
    g30: BSplineCurve PolesCount=3 KnotsCount=2 Degree=2 IsPeriodic=0
    g31: GeomPoint X=-7.19003 Y=-10 Z=0
    g32: GeomPoint X=-7.79258 Y=-12 Z=0
    g33: Circle CenterX=-8.70761 CenterY=-14 CenterZ=0 NormalX=0 NormalY=0 NormalZ=1 AngleXU=0 Radius=1
    g34: Circle CenterX=-9.33087 CenterY=-15.1837 CenterZ=0 NormalX=0 NormalY=0 NormalZ=1 AngleXU=0 Radius=1
    g35: Circle CenterX=-10.1571 CenterY=-16 CenterZ=0 NormalX=0 NormalY=0 NormalZ=1 AngleXU=0 Radius=1
    g36: BSplineCurve PolesCount=3 KnotsCount=2 Degree=2 IsPeriodic=0
    g37: GeomPoint X=-8.70761 Y=-14 Z=0
    g38: GeomPoint X=-10.1571 Y=-16 Z=0
    g39: Circle CenterX=-12.8401 CenterY=-17.6958 CenterZ=0 NormalX=0 NormalY=0 NormalZ=1 AngleXU=0 Radius=1
    g40: Circle CenterX=-13.3521 CenterY=-17.9027 CenterZ=0 NormalX=0 NormalY=0 NormalZ=1 AngleXU=0 Radius=1
    g41: Circle CenterX=-14 CenterY=-18 CenterZ=0 NormalX=0 NormalY=0 NormalZ=1 AngleXU=0 Radius=1
    g42: BSplineCurve PolesCount=3 KnotsCount=2 Degree=2 IsPeriodic=0
    g43: GeomPoint X=-12.8401 Y=-17.6958 Z=0
    g44: GeomPoint X=-14 Y=-18 Z=0
    g45: LineSegment StartX=-6.2 StartY=0 StartZ=0 EndX=-7.2 EndY=0 EndZ=0
    g46: LineSegment StartX=-7.2 StartY=0 StartZ=0 EndX=-7.2 EndY=-2 EndZ=0
    g47: LineSegment StartX=-7.2 StartY=-2 StartZ=0 EndX=-6.2215 EndY=-2 EndZ=0
    g48: LineSegment StartX=-6.32538 StartY=-4 StartZ=0 EndX=-7.65538 EndY=-4 EndZ=0
    g49: LineSegment StartX=-7.65538 StartY=-4 StartZ=0 EndX=-7.65538 EndY=-5.99526 EndZ=0
    g50: LineSegment StartX=-7.65538 StartY=-5.99526 StartZ=0 EndX=-6.48644 EndY=-5.99526 EndZ=0
    g51: LineSegment StartX=-6.77343 StartY=-8 StartZ=0 EndX=-8.43343 EndY=-8 EndZ=0
    g52: LineSegment StartX=-8.43343 StartY=-8 StartZ=0 EndX=-8.43343 EndY=-10 EndZ=0
    g53: LineSegment StartX=-8.43343 StartY=-10 StartZ=0 EndX=-7.19003 EndY=-10 EndZ=0
  constraints (112):
    c: Horizontal(g0)
    c: Distance(g0) = 2
    c: Block(g0)
    c: Vertical(g1)
    c: Coincident(g2,g0)
    c: Vertical(g2)
    c: Block(g2)
    c: Coincident(g6,g2)
    c: Weight(g3) = 1
    c: Equal(g3,g4)
    c: Equal(g3,g5)
    c: InternalAlignment(g3,g6)
    c: InternalAlignment(g4,g6)
    c: InternalAlignment(g5,g6)
    c: InternalAlignment(g7,g6)
    c: InternalAlignment(g8,g6)
    c: Block(g6)
    c: Coincident(g9,g1)
    c: Coincident(g9,g6)
    c: Horizontal(g9)
    c: Vertical(g10)
    c: Block(g10)
    c: Horizontal(g11)
    c: Block(g11)
    c: Coincident(g12,g10)
    c: Horizontal(g12)
    c: Block(g12)
    c: Coincident(g13,g11)
    c: Vertical(g13)
    c: Block(g13)
    c: Coincident(g14,g10)
    c: Horizontal(g14)
    c: Block(g14)
    c: Block(g9)
    c: Block(g1)
    c: Weight(g15) = 1
    c: Equal(g15,g16)
    c: Equal(g15,g17)
    c: InternalAlignment(g15,g18)
    c: InternalAlignment(g16,g18)
    c: InternalAlignment(g17,g18)
    c: InternalAlignment(g19,g18)
    c: InternalAlignment(g20,g18)
    c: Weight(g21) = 1
    c: Equal(g21,g22)
    c: Equal(g21,g23)
    c: InternalAlignment(g21,g24)
    c: InternalAlignment(g22,g24)
    c: InternalAlignment(g23,g24)
    c: InternalAlignment(g25,g24)
    c: InternalAlignment(g26,g24)
    c: Weight(g27) = 1
    c: Equal(g27,g28)
    c: Equal(g27,g29)
    c: Coincident(g30,g14)
    c: InternalAlignment(g27,g30)
    c: InternalAlignment(g28,g30)
    c: InternalAlignment(g29,g30)
    c: InternalAlignment(g31,g30)
    c: InternalAlignment(g32,g30)
    c: Coincident(g36,g12)
    c: Weight(g33) = 1
    c: Equal(g33,g34)
    c: Equal(g33,g35)
    c: Coincident(g36,g11)
    c: InternalAlignment(g33,g36)
    c: InternalAlignment(g34,g36)
    c: InternalAlignment(g35,g36)
    c: InternalAlignment(g37,g36)
    c: InternalAlignment(g38,g36)
    c: Coincident(g42,g13)
    c: Weight(g39) = 1
    c: Equal(g39,g40)
    c: Equal(g39,g41)
    c: Coincident(g42,g1)
    c: InternalAlignment(g39,g42)
    c: InternalAlignment(g40,g42)
    c: InternalAlignment(g41,g42)
    c: InternalAlignment(g43,g42)
    c: InternalAlignment(g44,g42)
    c: Block(g18)
    c: Block(g24)
    c: Block(g30)
    c: Block(g36)
    c: Block(g42)
    c: Horizontal(g45)
    c: Coincident(g45,g0)
    c: Vertical(g46)
    c: Coincident(g46,g45)
    c: Coincident(g47,g46)
    c: Coincident(g47,g18)
    c: Horizontal(g47)
    c: Block(g46)
    c: Coincident(g48,g18)
    c: Horizontal(g48)
    c: Distance(g48) = 1.33
    c: Vertical(g49)
    c: Coincident(g49,g48)
    c: Coincident(g50,g49)
    c: Coincident(g50,g24)
    c: Horizontal(g50)
    c: Tangent(g50,g22)
    c: Horizontal(g51)
    c: Coincident(g51,g24)
    c: Block(g51)
    c: Vertical(g52)
    c: Block(g52)
    c: Coincident(g52,g51)
    c: Coincident(g53,g52)
    c: Coincident(g53,g30)
    c: Horizontal(g53)
    c: Distance(g1) = 8.5
FEATURE [Part::Feature] Face024
  shape: bbox 9.8 x 26.5 x 2e-07 mm, 1 faces, 0 solids (baked)
FEATURE [Part::Revolution] Revolve024
  Angle = 360
  Axis = (0,1,0)
  Base = (0,0,0)
  FaceMakerClass = Part::FaceMakerBullseye
  Placement = pos=(0,0,0) rot=(0,0,1;1.5708rad)
  Solid = false
  Source = -> Face024
  Symmetric = false
FEATURE [Part::Feature] Face025
  shape: bbox 9.8 x 26.5 x 2e-07 mm, 1 faces, 0 solids (baked)
FEATURE [Part::Revolution] Revolve025
  Angle = 360
  Axis = (0,1,0)
  Base = (0,0,0)
  FaceMakerClass = Part::FaceMakerBullseye
  Placement = pos=(0,0,0) rot=(0,0,1;1.5708rad)
  Solid = false
  Source = -> Face025
  Symmetric = false
FEATURE [Part::MultiFuse] Fusion033
  Placement = pos=(-18,19,36) rot=(0,0,1;0rad)
  Shapes = -> [Revolve025,Revolve024]
FEATURE [Part::Cylinder] Cylinder014
  Angle = 360
  AttacherType = Attacher::AttachEngine3D
  Height = 20
  Placement = pos=(0,0,36.15) rot=(0,0,1;0rad)
  Radius = 14.3
FEATURE [Part::Cylinder] Cylinder015
  Angle = 360
  AttacherType = Attacher::AttachEngine3D
  Height = 10
  Placement = pos=(0,0,36.15) rot=(0,0,1;0rad)
  Radius = 4
FEATURE [Part::MultiFuse] Fusion034  label="removeToCreteHoleForPlugHousing004"
  Placement = pos=(-42,19,36) rot=(0,1,0;1.5708rad)
  Shapes = -> [Cylinder014,Cylinder015]
FEATURE [Part::Cut] Cut008  label="top004"
  Base = -> Cut004
  Placement = pos=(-1,0,0) rot=(0,0,1;0rad)
  Tool = -> Fusion034
FEATURE [Part::Box] Box005  label="Cube005"
  AttacherType = Attacher::AttachEngine3D
  Height = 28
  Length = 3
  Placement = pos=(110.7,19,22) rot=(0,0,1;0rad)
  Width = 15.7
FEATURE [Part::Cylinder] Cylinder016
  Angle = 360
  AttacherType = Attacher::AttachEngine3D
  Height = 10
  Placement = pos=(0,0,36.15) rot=(0,0,1;0rad)
  Radius = 4
FEATURE [Part::Cylinder] Cylinder017
  Angle = 360
  AttacherType = Attacher::AttachEngine3D
  Height = 20
  Placement = pos=(0,0,36.15) rot=(0,0,1;0rad)
  Radius = 10.3
FEATURE [Part::MultiFuse] Fusion035  label="removeToCreteHoleForPlugHousing005"
  Placement = pos=(70,19,36) rot=(0,1,0;1.5708rad)
  Shapes = -> [Cylinder017,Cylinder016]
FEATURE [Part::Cut] Cut009  label="plugHousingTab001"
  Base = -> Box005
  Placement = pos=(-107.4,-14,0) rot=(0,0,1;0rad)
  Tool = -> Fusion035
FEATURE [Part::Box] Box006  label="Cube006"
  AttacherType = Attacher::AttachEngine3D
  Height = 28
  Length = 3
  Placement = pos=(110.7,19,22) rot=(0,0,1;0rad)
  Width = 15.7
FEATURE [Part::Cylinder] Cylinder018
  Angle = 360
  AttacherType = Attacher::AttachEngine3D
  Height = 10
  Placement = pos=(0,0,36.15) rot=(0,0,1;0rad)
  Radius = 4
FEATURE [Part::Cylinder] Cylinder019
  Angle = 360
  AttacherType = Attacher::AttachEngine3D
  Height = 20
  Placement = pos=(0,0,36.15) rot=(0,0,1;0rad)
  Radius = 10.3
FEATURE [Part::MultiFuse] Fusion036  label="removeToCreteHoleForPlugHousing006"
  Placement = pos=(70,19,36) rot=(0,1,0;1.5708rad)
  Shapes = -> [Cylinder019,Cylinder018]
FEATURE [Part::Cut] Cut010  label="plugHousingTab002"
  Base = -> Box006
  Placement = pos=(-107.4,-14,0) rot=(0,0,1;0rad)
  Tool = -> Fusion036
FEATURE [Part::MultiFuse] Fusion037
  Placement = pos=(9.6,23,0) rot=(0,0,1;3.14159rad)
  Shapes = -> [Cut009,Cut010]
FEATURE [Part::Box] Box  label="Cube"
  AttacherType = Attacher::AttachEngine3D
  Height = 10
  Length = 3
  Placement = pos=(3.3,4,12) rot=(0,0,1;0rad)
  Width = 10
FEATURE [Part::Fillet] Fillet004
  Base = -> Fusion028
  Edges = 1 edges r=2: [Edge25]
FEATURE [Part::Fillet] Fillet005  label="plugHousing046"
  Base = -> Fillet004
  Edges = 1 edges r=2: [Edge8]
FEATURE [Part::Fillet] Fillet006
  Base = -> Box
  Edges = 1 edges r=2: [Edge11]
FEATURE [Part::Box] Box007  label="Cube007"
  AttacherType = Attacher::AttachEngine3D
  Height = 10
  Length = 3
  Placement = pos=(3.3,4,50) rot=(0,0,1;0rad)
  Width = 10
FEATURE [Part::Fillet] Fillet007
  Base = -> Box007
  Edges = 1 edges r=2: [Edge12]
FEATURE [Part::Box] Box008  label="Cube008"
  AttacherType = Attacher::AttachEngine3D
  Height = 28
  Length = 4
  Placement = pos=(5,0,22) rot=(0,0,1;0rad)
  Width = 10
FEATURE [Part::Fillet] Fillet008
  Base = -> Box008
  Edges = 1 edges r=1: [Edge7]
FEATURE [Part::Fillet] Fillet009
  Base = -> Fillet008
  Edges = 1 edges r=2: [Edge5]
FEATURE [Part::Fillet] Fillet010
  Base = -> Fillet009
  Edges = 1 edges r=2: [Edge2]
FEATURE [Sketcher::SketchObject] Sketch009  label="topSketch003"
  FullyConstrained = true
  sketch-geometry (4):
    g0: LineSegment StartX=16.8446 StartY=31.512 StartZ=0 EndX=16.3251 EndY=34.4666 EndZ=0
    g1: ArcOfCircle CenterX=19 CenterY=19.2524 CenterZ=0 NormalX=0 NormalY=0 NormalZ=1 AngleXU=0 Radius=15.4476 StartAngle=1.74483 EndAngle=2.72717
    g2: ArcOfCircle CenterX=19 CenterY=19.2524 CenterZ=0 NormalX=0 NormalY=0 NormalZ=1 AngleXU=0 Radius=12.4476 StartAngle=1.74483 EndAngle=2.73189
    g3: LineSegment StartX=4.86004 StartY=25.4725 StartZ=0 EndX=7.58253 EndY=24.2107 EndZ=0
  constraints (7):
    c: Block(g0)
    c: Coincident(g1,g0)
    c: Coincident(g2,g0)
    c: Coincident(g3,g1)
    c: Coincident(g3,g2)
    c: Block(g1)
    c: Block(g2)
FEATURE [Part::Extrusion] Extrude008
  Base = -> Sketch009
  Dir = (0,0,1)
  DirMode = 2
  FaceMakerClass = Part::FaceMakerBullseye
  LengthFwd = 10
  LengthRev = 0
  Placement = pos=(0,0,31) rot=(0,0,1;0rad)
  Solid = true
  Symmetric = false
FEATURE [Part::Cylinder] Cylinder020
  Angle = 360
  AttacherType = Attacher::AttachEngine3D
  Height = 20
  Placement = pos=(0,0,36.15) rot=(0,0,1;0rad)
  Radius = 8.2
FEATURE [Part::Cylinder] Cylinder021
  Angle = 360
  AttacherType = Attacher::AttachEngine3D
  Height = 10
  Placement = pos=(0,0,36.15) rot=(0,0,1;0rad)
  Radius = 4
FEATURE [Part::MultiFuse] Fusion038  label="removeToCreteHoleForPlugHousing007"
  Placement = pos=(-42,19,36) rot=(0,1,0;1.5708rad)
  Shapes = -> [Cylinder020,Cylinder021]
FEATURE [Part::Cut] Cut011
  Base = -> Extrude008
  Tool = -> Fusion038
FEATURE [Part::Fillet] Fillet011
  Base = -> Cut011
  Edges = 1 edges r=2: [Edge1]
FEATURE [Part::Fillet] Fillet012
  Base = -> Fillet011
  Edges = 1 edges r=2.5: [Edge1]
FEATURE [Part::Fillet] Fillet013
  Base = -> Fillet012
  Edges = 1 edges r=2.5: [Edge2]
FEATURE [Part::Box] Box010  label="Cube010"
  AttacherType = Attacher::AttachEngine3D
  Height = 16
  Length = 8
  Placement = pos=(12.7,31.52,28) rot=(0,0,1;0rad)
  Width = 4
FEATURE [Sketcher::SketchObject] Sketch010  label="topSketch004"
  FullyConstrained = true
  sketch-geometry (4):
    g0: LineSegment StartX=16.8446 StartY=31.512 StartZ=0 EndX=16.3251 EndY=34.4666 EndZ=0
    g1: ArcOfCircle CenterX=19 CenterY=19.2524 CenterZ=0 NormalX=0 NormalY=0 NormalZ=1 AngleXU=0 Radius=15.4476 StartAngle=1.74483 EndAngle=2.72717
    g2: ArcOfCircle CenterX=19 CenterY=19.2524 CenterZ=0 NormalX=0 NormalY=0 NormalZ=1 AngleXU=0 Radius=12.4476 StartAngle=1.74483 EndAngle=2.73189
    g3: LineSegment StartX=4.86004 StartY=25.4725 StartZ=0 EndX=7.58253 EndY=24.2107 EndZ=0
  constraints (7):
    c: Block(g0)
    c: Coincident(g1,g0)
    c: Coincident(g2,g0)
    c: Coincident(g3,g1)
    c: Coincident(g3,g2)
    c: Block(g1)
    c: Block(g2)
FEATURE [Part::Cylinder] Cylinder022
  Angle = 360
  AttacherType = Attacher::AttachEngine3D
  Height = 10
  Placement = pos=(0,0,36.15) rot=(0,0,1;0rad)
  Radius = 4
FEATURE [Sketcher::SketchObject] Sketch011  label="topSketch005"
  FullyConstrained = true
  sketch-geometry (4):
    g0: LineSegment StartX=16.8446 StartY=31.512 StartZ=0 EndX=16.3251 EndY=34.4666 EndZ=0
    g1: ArcOfCircle CenterX=19 CenterY=19.2524 CenterZ=0 NormalX=0 NormalY=0 NormalZ=1 AngleXU=0 Radius=15.4476 StartAngle=1.74483 EndAngle=2.72717
    g2: ArcOfCircle CenterX=19 CenterY=19.2524 CenterZ=0 NormalX=0 NormalY=0 NormalZ=1 AngleXU=0 Radius=12.4476 StartAngle=1.74483 EndAngle=2.73189
    g3: LineSegment StartX=4.86004 StartY=25.4725 StartZ=0 EndX=7.58253 EndY=24.2107 EndZ=0
  constraints (7):
    c: Block(g0)
    c: Coincident(g1,g0)
    c: Coincident(g2,g0)
    c: Coincident(g3,g1)
    c: Coincident(g3,g2)
    c: Block(g1)
    c: Block(g2)
FEATURE [Part::Extrusion] Extrude010
  Base = -> Sketch011
  Dir = (0,0,1)
  DirMode = 2
  FaceMakerClass = Part::FaceMakerBullseye
  LengthFwd = 10.6
  LengthRev = 0
  Placement = pos=(0,0,31) rot=(0,0,1;0rad)
  Solid = true
  Symmetric = false
FEATURE [Part::Cylinder] Cylinder023
  Angle = 360
  AttacherType = Attacher::AttachEngine3D
  Height = 20
  Placement = pos=(0,0,36.15) rot=(0,0,1;0rad)
  Radius = 8.2
FEATURE [Part::MultiFuse] Fusion039  label="removeToCreteHoleForPlugHousing008"
  Placement = pos=(-42,19,36) rot=(0,1,0;1.5708rad)
  Shapes = -> [Cylinder023,Cylinder022]
FEATURE [Part::Cut] Cut012
  Base = -> Extrude010
  Placement = pos=(0,0,-0.3) rot=(0,0,1;0rad)
  Tool = -> Fusion039
FEATURE [Part::Cut] Cut013
  Base = -> Box010
  Tool = -> Cut012
FEATURE [Part::Fillet] Fillet014
  Base = -> Cut013
  Edges = 1 edges r=0.7: [Edge13]
FEATURE [Part::Fillet] Fillet015
  Base = -> Fillet014
  Edges = 1 edges r=0.7: [Edge13]
FEATURE [Part::Fillet] Fillet016
  Base = -> Fillet015
  Edges = 1 edges r=0.7: [Edge16]
FEATURE [Part::Fillet] Fillet017
  Base = -> Fillet016
  Edges = 1 edges r=0.7: [Edge11]
FEATURE [Part::Fillet] Fillet018
  Base = -> Fillet017
  Edges = 1 edges r=0.7: [Edge10]
FEATURE [Part::Fillet] Fillet019
  Base = -> Fillet018
  Edges = 1 edges r=1.2: [Edge5]
FEATURE [Part::Fillet] Fillet020
  Base = -> Fillet019
  Edges = 1 edges r=1.2: [Edge12]
FEATURE [Part::Fillet] Fillet021
  Base = -> Fillet020
  Edges = 1 edges r=2: [Edge1]
  Placement = pos=(0.3,0,0) rot=(0,0,1;0rad)
FEATURE [Part::MultiFuse] Fusion040  label="top005"
  Shapes = -> [Cut008,Fillet021]
FEATURE [Part::MultiFuse] Fusion041  label="wireHolder"
  Shapes = -> [Fusion033,Fillet013]
FEATURE [Part::MultiFuse] Fusion042
  Shapes = -> [Fillet007,Fusion041]
FEATURE [Part::MultiFuse] Fusion043  label="wireHolder001"
  Shapes = -> [Fusion042,Fillet010]
FEATURE [Part::MultiFuse] Fusion044  label="wireHolder002"
  Shapes = -> [Fillet006,Fusion037,Fusion043]
FEATURE [Part::Feature] Face026
  shape: bbox 11 x 6 x 2e-07 mm, 1 faces, 0 solids (baked)
FEATURE [Part::Revolution] Revolve026
  Angle = 360
  Axis = (0,1,0)
  Base = (0,0,0)
  FaceMakerClass = Part::FaceMakerBullseye
  Placement = pos=(30.3,-1,19.7) rot=(0,0,1;0rad)
  Solid = false
  Source = -> Face026
  Symmetric = false
FEATURE [Sketcher::SketchObject] Sketch013  label="topSketch006"
  FullyConstrained = true
  sketch-geometry (13):
    g0: LineSegment StartX=117 StartY=19 StartZ=0 EndX=117 EndY=38 EndZ=0
    g1: ArcOfCircle CenterX=98 CenterY=19 CenterZ=0 NormalX=0 NormalY=0 NormalZ=1 AngleXU=0 Radius=19 StartAngle=5.7297 EndAngle=6.28319
    g2: LineSegment StartX=0 StartY=3 StartZ=0 EndX=0 EndY=19 EndZ=0
    g3: LineSegment StartX=19 StartY=38 StartZ=0 EndX=117 EndY=38 EndZ=0
    g4: ArcOfCircle CenterX=19 CenterY=19 CenterZ=0 NormalX=0 NormalY=0 NormalZ=1 AngleXU=0 Radius=19 StartAngle=1.5708 EndAngle=3.14159
    g5: ArcOfCircle CenterX=19 CenterY=19 CenterZ=0 NormalX=0 NormalY=0 NormalZ=1 AngleXU=0 Radius=16 StartAngle=1.5708 EndAngle=3.14159
    g6: ArcOfCircle CenterX=98 CenterY=19 CenterZ=0 NormalX=0 NormalY=0 NormalZ=1 AngleXU=0 Radius=16 StartAngle=5.60905 EndAngle=6.28319
    g7: LineSegment StartX=114 StartY=19 StartZ=0 EndX=114 EndY=35 EndZ=0
    g8: LineSegment StartX=110.5 StartY=9.01251 StartZ=0 EndX=114.163 EndY=9.01251 EndZ=0
    g9: LineSegment StartX=114 StartY=35 StartZ=0 EndX=19 EndY=35 EndZ=0
    g10: LineSegment StartX=0 StartY=3 StartZ=0 EndX=0 EndY=0 EndZ=0
    g11: LineSegment StartX=3 StartY=0 StartZ=0 EndX=0 EndY=0 EndZ=0
    g12: LineSegment StartX=3 StartY=19 StartZ=0 EndX=3 EndY=0 EndZ=0
  constraints (33):
    c: Vertical(g0)
    c: Distance(g0) = 19
    c: Block(g0)
    c: Coincident(g1,g0)
    c: Block(g1)
    c: Vertical(g2)
    c: Block(g2)
    c: Coincident(g3,g0)
    c: Horizontal(g3)
    c: Distance(g3) = 98
    c: Coincident(g4,g3)
    c: Coincident(g4,g2)
    c: Block(g4)
    c: Coincident(g5,g4)
    c: Coincident(g6,g1)
    c: Block(g6)
    c: Block(g5)
    c: Coincident(g7,g6)
    c: Vertical(g7)
    c: Coincident(g8,g6)
    c: Coincident(g8,g1)
    c: Coincident(g9,g7)
    c: Coincident(g9,g5)
    c: Horizontal(g9)
    c: Tangent(g9,g5)
    c: Coincident(g10,g2)
    c: Distance(g10) = 3
    c: Vertical(g10)
    c: Coincident(g11,g10)
    c: Horizontal(g11)
    c: Coincident(g12,g5)
    c: Coincident(g12,g11)
    c: Vertical(g12)
FEATURE [Part::Extrusion] Extrude011  label="top006"
  Base = -> Sketch013
  Dir = (0,0,1)
  DirMode = 2
  FaceMakerClass = Part::FaceMakerBullseye
  LengthFwd = 72
  LengthRev = 0
  Solid = true
  Symmetric = false
FEATURE [Sketcher::SketchObject] Sketch014
  FullyConstrained = true
  MapMode = 3
  Placement = pos=(0,0,0) rot=(1,0,0;1.5708rad)
  Support = -> [Extrude011]
  sketch-geometry (8):
    g0: Circle CenterX=80.351 CenterY=-67.6202 CenterZ=0 NormalX=0 NormalY=0 NormalZ=1 AngleXU=0 Radius=2
    g1: Circle CenterX=80.351 CenterY=-67.6202 CenterZ=0 NormalX=0 NormalY=0 NormalZ=1 AngleXU=0 Radius=3
    g2: Circle CenterX=80.351 CenterY=-4.92017 CenterZ=0 NormalX=0 NormalY=0 NormalZ=1 AngleXU=0 Radius=2
    g3: Circle CenterX=80.351 CenterY=-4.92017 CenterZ=0 NormalX=0 NormalY=0 NormalZ=1 AngleXU=0 Radius=3
    g4: Circle CenterX=23.851 CenterY=-4.92017 CenterZ=0 NormalX=0 NormalY=0 NormalZ=1 AngleXU=0 Radius=2
    g5: Circle CenterX=23.851 CenterY=-4.92017 CenterZ=0 NormalX=0 NormalY=0 NormalZ=1 AngleXU=0 Radius=3
    g6: Circle CenterX=23.851 CenterY=-67.6202 CenterZ=0 NormalX=0 NormalY=0 NormalZ=1 AngleXU=0 Radius=2
    g7: Circle CenterX=23.851 CenterY=-67.6202 CenterZ=0 NormalX=0 NormalY=0 NormalZ=1 AngleXU=0 Radius=3
  constraints (8):
    c: Block(g3)
    c: Block(g2)
    c: Block(g1)
    c: Block(g0)
    c: Block(g6)
    c: Block(g7)
    c: Block(g4)
    c: Block(g5)
FEATURE [Part::Feature] Face027
  shape: bbox 11 x 6 x 2e-07 mm, 1 faces, 0 solids (baked)
FEATURE [Part::Revolution] Revolve027
  Angle = 360
  Axis = (0,1,0)
  Base = (0,0,0)
  FaceMakerClass = Part::FaceMakerBullseye
  Placement = pos=(30.3,-1,51.7) rot=(0,0,1;0rad)
  Solid = false
  Source = -> Face027
  Symmetric = false
FEATURE [Part::Feature] Face028
  shape: bbox 11 x 6 x 2e-07 mm, 1 faces, 0 solids (baked)
FEATURE [Part::Revolution] Revolve028
  Angle = 360
  Axis = (0,1,0)
  Base = (0,0,0)
  FaceMakerClass = Part::FaceMakerBullseye
  Placement = pos=(62.3,-1,19.7) rot=(0,0,1;0rad)
  Solid = false
  Source = -> Face028
  Symmetric = false
FEATURE [Part::Feature] Face029
  shape: bbox 11 x 6 x 2e-07 mm, 1 faces, 0 solids (baked)
FEATURE [Part::Revolution] Revolve029
  Angle = 360
  Axis = (0,1,0)
  Base = (0,0,0)
  FaceMakerClass = Part::FaceMakerBullseye
  Placement = pos=(62.3,-1,51.7) rot=(0,0,1;0rad)
  Solid = false
  Source = -> Face029
  Symmetric = false
FEATURE [Part::Feature] Wire
  shape: bbox 11 x 5.2 x 2e-07 mm, 0 faces, 0 solids (baked)
FEATURE [Part::Revolution] Revolve030
  Angle = 360
  Axis = (0,1,0)
  Base = (0,0,0)
  FaceMakerClass = Part::FaceMakerBullseye
  Placement = pos=(30.3,38,19.7) rot=(0,0,1;0rad)
  Solid = true
  Source = -> Wire
  Symmetric = false
FEATURE [Part::Feature] Wire001
  shape: bbox 11 x 5.2 x 2e-07 mm, 0 faces, 0 solids (baked)
FEATURE [Part::Revolution] Revolve031
  Angle = 360
  Axis = (0,1,0)
  Base = (0,0,0)
  FaceMakerClass = Part::FaceMakerBullseye
  Placement = pos=(30.3,38,51.7) rot=(0,0,1;0rad)
  Solid = true
  Source = -> Wire001
  Symmetric = false
FEATURE [Part::Feature] Wire002
  shape: bbox 11 x 5.2 x 2e-07 mm, 0 faces, 0 solids (baked)
FEATURE [Part::Revolution] Revolve032
  Angle = 360
  Axis = (0,1,0)
  Base = (0,0,0)
  FaceMakerClass = Part::FaceMakerBullseye
  Placement = pos=(62.3,38,51.7) rot=(0,0,1;0rad)
  Solid = true
  Source = -> Wire002
  Symmetric = false
FEATURE [Part::Feature] Wire003
  shape: bbox 11 x 5.2 x 2e-07 mm, 0 faces, 0 solids (baked)
FEATURE [Part::Revolution] Revolve033
  Angle = 360
  Axis = (0,1,0)
  Base = (0,0,0)
  FaceMakerClass = Part::FaceMakerBullseye
  Placement = pos=(62.3,38,19.7) rot=(0,0,1;0rad)
  Solid = true
  Source = -> Wire003
  Symmetric = false
FEATURE [Part::MultiFuse] Fusion045  label="altRandScrewHousing"
  Shapes = -> [Revolve029,Revolve027,Revolve028,Revolve026]
FEATURE [Part::MultiFuse] Fusion046  label="fanScrewHousing"
  Shapes = -> [Revolve033,Revolve032,Revolve031,Revolve030]
FEATURE [Sketcher::SketchObject] Sketch015
  FullyConstrained = true
  sketch-geometry (17):
    g0: Circle CenterX=-3.5 CenterY=23.5 CenterZ=0 NormalX=0 NormalY=0 NormalZ=1 AngleXU=0 Radius=1
    g1: Circle CenterX=-1 CenterY=15.25 CenterZ=0 NormalX=0 NormalY=0 NormalZ=1 AngleXU=0 Radius=1
    g2: Circle CenterX=-3.5 CenterY=7 CenterZ=0 NormalX=0 NormalY=0 NormalZ=1 AngleXU=0 Radius=1
    g3: BSplineCurve PolesCount=3 KnotsCount=2 Degree=2 IsPeriodic=0
    g4: GeomPoint X=-3.5 Y=23.5 Z=0
    g5: GeomPoint X=-3.5 Y=7 Z=0
    g6: Circle CenterX=-4.8 CenterY=30.5 CenterZ=0 NormalX=0 NormalY=0 NormalZ=1 AngleXU=0 Radius=1
    g7: Circle CenterX=-3.5 CenterY=30.5 CenterZ=0 NormalX=0 NormalY=0 NormalZ=1 AngleXU=0 Radius=1
    g8: Circle CenterX=-3.5 CenterY=29.2 CenterZ=0 NormalX=0 NormalY=0 NormalZ=1 AngleXU=0 Radius=1
    g9: BSplineCurve PolesCount=3 KnotsCount=2 Degree=2 IsPeriodic=0
    g10: GeomPoint X=-4.8 Y=30.5 Z=0
    g11: GeomPoint X=-3.5 Y=29.2 Z=0
    g12: LineSegment StartX=-3.5 StartY=29.2 StartZ=0 EndX=-3.5 EndY=23.5 EndZ=0
    g13: LineSegment StartX=-4.8 StartY=30.5 StartZ=0 EndX=0 EndY=30.5 EndZ=0
    g14: LineSegment StartX=-3.5 StartY=0.3 StartZ=0 EndX=0 EndY=0.3 EndZ=0
    g15: LineSegment StartX=-3.5 StartY=0.3 StartZ=0 EndX=-3.5 EndY=7 EndZ=0
    g16: LineSegment StartX=0 StartY=0.3 StartZ=0 EndX=0 EndY=30.5 EndZ=0
  constraints (33):
    c: Weight(g0) = 1
    c: Equal(g0,g1)
    c: Equal(g0,g2)
    c: InternalAlignment(g0,g3)
    c: InternalAlignment(g1,g3)
    c: InternalAlignment(g2,g3)
    c: InternalAlignment(g4,g3)
    c: InternalAlignment(g5,g3)
    c: Block(g3)
    c: Weight(g6) = 1
    c: Equal(g6,g7)
    c: Equal(g6,g8)
    c: InternalAlignment(g6,g9)
    c: InternalAlignment(g7,g9)
    c: InternalAlignment(g8,g9)
    c: InternalAlignment(g10,g9)
    c: InternalAlignment(g11,g9)
    c: Block(g9)
    c: Coincident(g12,g9)
    c: Coincident(g12,g3)
    c: Vertical(g12)
    c: Coincident(g13,g9)
    c: Horizontal(g13)
    c: Distance(g13) = 4.8
    c: Horizontal(g14)
    c: Block(g14)
    c: Coincident(g15,g14)
    c: Coincident(g15,g3)
    c: Vertical(g15)
    c: Coincident(g16,g14)
    c: Coincident(g16,g13)
    c: Vertical(g16)
    c: Tangent(g16,g1)
FEATURE [Sketcher::SketchObject] Sketch016
  FullyConstrained = true
  sketch-geometry (16):
    g0: Circle CenterX=-3.5 CenterY=23.5 CenterZ=0 NormalX=0 NormalY=0 NormalZ=1 AngleXU=0 Radius=1
    g1: Circle CenterX=-1 CenterY=15.25 CenterZ=0 NormalX=0 NormalY=0 NormalZ=1 AngleXU=0 Radius=1
    g2: Circle CenterX=-3.5 CenterY=7 CenterZ=0 NormalX=0 NormalY=0 NormalZ=1 AngleXU=0 Radius=1
    g3: BSplineCurve PolesCount=3 KnotsCount=2 Degree=2 IsPeriodic=0
    g4: GeomPoint X=-3.5 Y=23.5 Z=0
    g5: GeomPoint X=-3.5 Y=7 Z=0
    g6: LineSegment StartX=-3.5 StartY=28.2 StartZ=0 EndX=-3.5 EndY=23.5 EndZ=0
    g7: LineSegment StartX=0 StartY=29.5 StartZ=0 EndX=0 EndY=30 EndZ=0
    g8: LineSegment StartX=-3.5 StartY=28.2 StartZ=0 EndX=-3.5 EndY=30 EndZ=0
    g9: LineSegment StartX=0 StartY=30 StartZ=0 EndX=0 EndY=30.5 EndZ=0
    g10: LineSegment StartX=0 StartY=30.5 StartZ=0 EndX=-3.5 EndY=30.5 EndZ=0
    g11: LineSegment StartX=-3.5 StartY=30.5 StartZ=0 EndX=-3.5 EndY=30 EndZ=0
    g12: LineSegment StartX=0 StartY=29.5 StartZ=0 EndX=0 EndY=5 EndZ=0
    g13: LineSegment StartX=-3.5 StartY=0.3 StartZ=0 EndX=-3.5 EndY=7 EndZ=0
    g14: LineSegment StartX=-3.5 StartY=0.3 StartZ=0 EndX=0 EndY=0.3 EndZ=0
    g15: LineSegment StartX=0 StartY=5 StartZ=0 EndX=0 EndY=0.3 EndZ=0
  constraints (39):
    c: Weight(g0) = 1
    c: Equal(g0,g1)
    c: Equal(g0,g2)
    c: InternalAlignment(g0,g3)
    c: InternalAlignment(g1,g3)
    c: InternalAlignment(g2,g3)
    c: InternalAlignment(g4,g3)
    c: InternalAlignment(g5,g3)
    c: Block(g3)
    c: Coincident(g6,g3)
    c: Vertical(g6)
    c: Vertical(g7)
    c: Distance(g7) = 0.5
    c: Coincident(g8,g6)
    c: Vertical(g8)
    c: Block(g6)
    c: Block(g7)
    c: Vertical(g9)
    c: Equal(g7,g9) = 0.5
    c: Block(g9)
    c: Coincident(g9,g7)
    c: Horizontal(g10)
    c: Coincident(g10,g9)
    c: Coincident(g11,g10)
    c: Coincident(g11,g8)
    c: Vertical(g11)
    c: Block(g11)
    c: Coincident(g12,g7)
    c: Vertical(g12)
    c: Coincident(g13,g3)
    c: Vertical(g13)
    c: Distance(g13) = 6.7
    c: Coincident(g14,g13)
    c: Horizontal(g14)
    c: Block(g14)
    c: Coincident(g15,g12)
    c: Coincident(g15,g14)
    c: Vertical(g15)
    c: Block(g15)
FEATURE [Sketcher::SketchObject] Sketch017
  FullyConstrained = true
  sketch-geometry (11):
    g0: LineSegment StartX=-3.5 StartY=1e-16 StartZ=0 EndX=-1.6 EndY=1e-16 EndZ=0
    g1: LineSegment StartX=-1.6 StartY=1e-16 StartZ=0 EndX=-1.6 EndY=1.5 EndZ=0
    g2: LineSegment StartX=-3.5 StartY=1.5 StartZ=0 EndX=-1.6 EndY=1.5 EndZ=0
    g3: LineSegment StartX=-3.5 StartY=1e-16 StartZ=0 EndX=-4.8 EndY=1e-16 EndZ=0
    g4: Circle CenterX=-3.5 CenterY=1.3 CenterZ=0 NormalX=0 NormalY=0 NormalZ=1 AngleXU=0 Radius=1
    g5: Circle CenterX=-3.5 CenterY=1e-16 CenterZ=0 NormalX=0 NormalY=0 NormalZ=1 AngleXU=0 Radius=1
    g6: Circle CenterX=-4.8 CenterY=1e-16 CenterZ=0 NormalX=0 NormalY=0 NormalZ=1 AngleXU=0 Radius=1
    g7: BSplineCurve PolesCount=3 KnotsCount=2 Degree=2 IsPeriodic=0
    g8: GeomPoint X=-3.5 Y=1.3 Z=0
    g9: GeomPoint X=-4.8 Y=1e-16 Z=0
    g10: LineSegment StartX=-3.5 StartY=1.3 StartZ=0 EndX=-3.5 EndY=1.5 EndZ=0
  constraints (24):
    c: Horizontal(g0)
    c: Distance(g0) = 1.9
    c: Block(g0)
    c: Coincident(g1,g0)
    c: Vertical(g1)
    c: Coincident(g2,g1)
    c: Horizontal(g2)
    c: Coincident(g3,g0)
    c: Horizontal(g3)
    c: Distance(g3) = 1.3
    c: Weight(g4) = 1
    c: Equal(g4,g5)
    c: Coincident(g5,g0)
    c: Equal(g4,g6)
    c: Coincident(g7,g3)
    c: InternalAlignment(g4,g7)
    c: InternalAlignment(g5,g7)
    c: InternalAlignment(g6,g7)
    c: InternalAlignment(g8,g7)
    c: InternalAlignment(g9,g7)
    c: Coincident(g10,g7)
    c: Coincident(g10,g2)
    c: Vertical(g10)
    c: Block(g10)
FEATURE [Part::Feature] Face035
  shape: bbox 3.2 x 1.5 x 2e-07 mm, 1 faces, 0 solids (baked)
FEATURE [Part::Revolution] Revolve039  label="backCaseScrewRetainer"
  Angle = 360
  Axis = (0,1,0)
  Base = (0,0,0)
  FaceMakerClass = Part::FaceMakerBullseye
  Placement = pos=(12.5,3,62) rot=(0,0,1;0rad)
  Solid = false
  Source = -> Face035
  Symmetric = false
FEATURE [Part::Feature] Face036
  shape: bbox 3.2 x 1.5 x 2e-07 mm, 1 faces, 0 solids (baked)
FEATURE [Part::Feature] Face039
  shape: bbox 4.8 x 30.2 x 2e-07 mm, 1 faces, 0 solids (baked)
FEATURE [Part::Revolution] Revolve043  label="frontCaseScrewPost002"
  Angle = 360
  Axis = (0,1,0)
  Base = (0,0,0)
  FaceMakerClass = Part::FaceMakerBullseye
  Placement = pos=(89.5,4.5,3.5) rot=(0,0,1;0rad)
  Solid = false
  Source = -> Face039
  Symmetric = false
FEATURE [Part::Feature] Face042
  shape: bbox 4.8 x 30.2 x 2e-07 mm, 1 faces, 0 solids (baked)
FEATURE [Part::Revolution] Revolve046  label="frontCaseScrewPost003"
  Angle = 360
  Axis = (0,1,0)
  Base = (0,0,0)
  FaceMakerClass = Part::FaceMakerBullseye
  Placement = pos=(89.5,4.5,68.5) rot=(0,0,1;0rad)
  Solid = false
  Source = -> Face042
  Symmetric = false
FEATURE [Part::Feature] Face043
  shape: bbox 3.2 x 1.5 x 2e-07 mm, 1 faces, 0 solids (baked)
FEATURE [Part::Revolution] Revolve047  label="frontCaseScrewRetainer002"
  Angle = 360
  Axis = (0,1,0)
  Base = (0,0,0)
  FaceMakerClass = Part::FaceMakerBullseye
  Placement = pos=(89.5,3,68.5) rot=(0,0,1;0rad)
  Solid = false
  Source = -> Face043
  Symmetric = false
FEATURE [Part::Feature] Face044
  shape: bbox 3.2 x 1.5 x 2e-07 mm, 1 faces, 0 solids (baked)
FEATURE [Part::Revolution] Revolve048  label="frontCaseScrewRetainer003"
  Angle = 360
  Axis = (0,1,0)
  Base = (0,0,0)
  FaceMakerClass = Part::FaceMakerBullseye
  Placement = pos=(89.5,3,3.5) rot=(0,0,1;0rad)
  Solid = false
  Source = -> Face044
  Symmetric = false
FEATURE [App::MeasureDistance] Distance002  label="Distance: 1.67 mm"
  Distance = 1.66921
  P1 = (99.2361,4.7524,71.7)
  P2 = (99.2347,6.42161,71.7)
FEATURE [Sketcher::SketchObject] Sketch018
  FullyConstrained = true
  sketch-geometry (7):
    g0: LineSegment StartX=0 StartY=0 StartZ=0 EndX=0 EndY=6 EndZ=0
    g1: Circle CenterX=0 CenterY=0 CenterZ=0 NormalX=0 NormalY=0 NormalZ=1 AngleXU=0 Radius=1
    g2: Circle CenterX=8 CenterY=6 CenterZ=0 NormalX=0 NormalY=0 NormalZ=1 AngleXU=0 Radius=1
    g3: BSplineCurve PolesCount=3 KnotsCount=2 Degree=2 IsPeriodic=0
    g4: GeomPoint X=0 Y=0 Z=0
    g5: GeomPoint X=8 Y=6 Z=0
    g6: LineSegment StartX=0 StartY=6 StartZ=0 EndX=8 EndY=6 EndZ=0
  constraints (14):
    c: Coincident(g0,g-1)
    c: Distance(g0) = 6
    c: Vertical(g0)
    c: Coincident(g3,g0)
    c: Weight(g1) = 1
    c: Equal(g1,g2)
    c: InternalAlignment(g1,g3)
    c: InternalAlignment(g2,g3)
    c: InternalAlignment(g4,g3)
    c: InternalAlignment(g5,g3)
    c: Block(g3)
    c: Coincident(g6,g0)
    c: Coincident(g6,g3)
    c: Horizontal(g6)
FEATURE [Part::Extrusion] Extrude012  label="caseScrewPillarBracket"
  Base = -> Sketch018
  Dir = (0,0,1)
  DirMode = 2
  FaceMakerClass = Part::FaceMakerBullseye
  LengthFwd = 2.4
  LengthRev = 0
  Placement = pos=(15.76,29,8.8) rot=(0,1,0;0rad)
  Solid = true
  Symmetric = false
FEATURE [Sketcher::SketchObject] Sketch019
  FullyConstrained = true
  sketch-geometry (7):
    g0: LineSegment StartX=0 StartY=0 StartZ=0 EndX=0 EndY=6 EndZ=0
    g1: Circle CenterX=0 CenterY=0 CenterZ=0 NormalX=0 NormalY=0 NormalZ=1 AngleXU=0 Radius=1
    g2: Circle CenterX=8 CenterY=6 CenterZ=0 NormalX=0 NormalY=0 NormalZ=1 AngleXU=0 Radius=1
    g3: BSplineCurve PolesCount=3 KnotsCount=2 Degree=2 IsPeriodic=0
    g4: GeomPoint X=0 Y=0 Z=0
    g5: GeomPoint X=8 Y=6 Z=0
    g6: LineSegment StartX=0 StartY=6 StartZ=0 EndX=8 EndY=6 EndZ=0
  constraints (14):
    c: Coincident(g0,g-1)
    c: Distance(g0) = 6
    c: Vertical(g0)
    c: Coincident(g3,g0)
    c: Weight(g1) = 1
    c: Equal(g1,g2)
    c: InternalAlignment(g1,g3)
    c: InternalAlignment(g2,g3)
    c: InternalAlignment(g4,g3)
    c: InternalAlignment(g5,g3)
    c: Block(g3)
    c: Coincident(g6,g0)
    c: Coincident(g6,g3)
    c: Horizontal(g6)
FEATURE [Part::Extrusion] Extrude013  label="caseScrewPillarBracket001"
  Base = -> Sketch019
  Dir = (0,0,1)
  DirMode = 2
  FaceMakerClass = Part::FaceMakerBullseye
  LengthFwd = 2.4
  LengthRev = 0
  Placement = pos=(15.76,29,60.8) rot=(0,0,1;0rad)
  Solid = true
  Symmetric = false
FEATURE [Sketcher::SketchObject] Sketch020
  FullyConstrained = true
  sketch-geometry (7):
    g0: LineSegment StartX=0 StartY=0 StartZ=0 EndX=0 EndY=6 EndZ=0
    g1: Circle CenterX=0 CenterY=0 CenterZ=0 NormalX=0 NormalY=0 NormalZ=1 AngleXU=0 Radius=1
    g2: Circle CenterX=8 CenterY=6 CenterZ=0 NormalX=0 NormalY=0 NormalZ=1 AngleXU=0 Radius=1
    g3: BSplineCurve PolesCount=3 KnotsCount=2 Degree=2 IsPeriodic=0
    g4: GeomPoint X=0 Y=0 Z=0
    g5: GeomPoint X=8 Y=6 Z=0
    g6: LineSegment StartX=0 StartY=6 StartZ=0 EndX=8 EndY=6 EndZ=0
  constraints (14):
    c: Coincident(g0,g-1)
    c: Distance(g0) = 6
    c: Vertical(g0)
    c: Coincident(g3,g0)
    c: Weight(g1) = 1
    c: Equal(g1,g2)
    c: InternalAlignment(g1,g3)
    c: InternalAlignment(g2,g3)
    c: InternalAlignment(g4,g3)
    c: InternalAlignment(g5,g3)
    c: Block(g3)
    c: Coincident(g6,g0)
    c: Coincident(g6,g3)
    c: Horizontal(g6)
FEATURE [Part::Extrusion] Extrude014  label="caseScrewPillarBracket002"
  Base = -> Sketch020
  Dir = (0,0,1)
  DirMode = 2
  FaceMakerClass = Part::FaceMakerBullseye
  LengthFwd = 2.4
  LengthRev = 0
  Placement = pos=(13.7,29,13.26) rot=(0,1,0;-1.5708rad)
  Solid = true
  Symmetric = false
FEATURE [Sketcher::SketchObject] Sketch021
  FullyConstrained = true
  sketch-geometry (7):
    g0: LineSegment StartX=0 StartY=0 StartZ=0 EndX=0 EndY=6 EndZ=0
    g1: Circle CenterX=0 CenterY=0 CenterZ=0 NormalX=0 NormalY=0 NormalZ=1 AngleXU=0 Radius=1
    g2: Circle CenterX=8 CenterY=6 CenterZ=0 NormalX=0 NormalY=0 NormalZ=1 AngleXU=0 Radius=1
    g3: BSplineCurve PolesCount=3 KnotsCount=2 Degree=2 IsPeriodic=0
    g4: GeomPoint X=0 Y=0 Z=0
    g5: GeomPoint X=8 Y=6 Z=0
    g6: LineSegment StartX=0 StartY=6 StartZ=0 EndX=8 EndY=6 EndZ=0
  constraints (14):
    c: Coincident(g0,g-1)
    c: Distance(g0) = 6
    c: Vertical(g0)
    c: Coincident(g3,g0)
    c: Weight(g1) = 1
    c: Equal(g1,g2)
    c: InternalAlignment(g1,g3)
    c: InternalAlignment(g2,g3)
    c: InternalAlignment(g4,g3)
    c: InternalAlignment(g5,g3)
    c: Block(g3)
    c: Coincident(g6,g0)
    c: Coincident(g6,g3)
    c: Horizontal(g6)
FEATURE [Part::Extrusion] Extrude015  label="caseScrewPillarBracket003"
  Base = -> Sketch021
  Dir = (0,0,1)
  DirMode = 2
  FaceMakerClass = Part::FaceMakerBullseye
  LengthFwd = 2.4
  LengthRev = 0
  Placement = pos=(11.3,29,58.74) rot=(0,1,0;1.5708rad)
  Solid = true
  Symmetric = false
FEATURE [Sketcher::SketchObject] Sketch022
  FullyConstrained = true
  sketch-geometry (7):
    g0: LineSegment StartX=0 StartY=0 StartZ=0 EndX=0 EndY=6 EndZ=0
    g1: Circle CenterX=0 CenterY=0 CenterZ=0 NormalX=0 NormalY=0 NormalZ=1 AngleXU=0 Radius=1
    g2: Circle CenterX=8 CenterY=6 CenterZ=0 NormalX=0 NormalY=0 NormalZ=1 AngleXU=0 Radius=1
    g3: BSplineCurve PolesCount=3 KnotsCount=2 Degree=2 IsPeriodic=0
    g4: GeomPoint X=0 Y=0 Z=0
    g5: GeomPoint X=8 Y=6 Z=0
    g6: LineSegment StartX=0 StartY=6 StartZ=0 EndX=8 EndY=6 EndZ=0
  constraints (14):
    c: Coincident(g0,g-1)
    c: Distance(g0) = 6
    c: Vertical(g0)
    c: Coincident(g3,g0)
    c: Weight(g1) = 1
    c: Equal(g1,g2)
    c: InternalAlignment(g1,g3)
    c: InternalAlignment(g2,g3)
    c: InternalAlignment(g4,g3)
    c: InternalAlignment(g5,g3)
    c: Block(g3)
    c: Coincident(g6,g0)
    c: Coincident(g6,g3)
    c: Horizontal(g6)
FEATURE [Part::Extrusion] Extrude016  label="caseScrewPillarBracket004"
  Base = -> Sketch022
  Dir = (0,0,1)
  DirMode = 2
  FaceMakerClass = Part::FaceMakerBullseye
  LengthFwd = 2.4
  LengthRev = 0
  Placement = pos=(88.3,29,65.23) rot=(0,1,0;1.5708rad)
  Solid = true
  Symmetric = false
FEATURE [Sketcher::SketchObject] Sketch023
  FullyConstrained = true
  sketch-geometry (7):
    g0: LineSegment StartX=0 StartY=0 StartZ=0 EndX=0 EndY=6 EndZ=0
    g1: Circle CenterX=0 CenterY=0 CenterZ=0 NormalX=0 NormalY=0 NormalZ=1 AngleXU=0 Radius=1
    g2: Circle CenterX=8 CenterY=6 CenterZ=0 NormalX=0 NormalY=0 NormalZ=1 AngleXU=0 Radius=1
    g3: BSplineCurve PolesCount=3 KnotsCount=2 Degree=2 IsPeriodic=0
    g4: GeomPoint X=0 Y=0 Z=0
    g5: GeomPoint X=8 Y=6 Z=0
    g6: LineSegment StartX=0 StartY=6 StartZ=0 EndX=8 EndY=6 EndZ=0
  constraints (14):
    c: Coincident(g0,g-1)
    c: Distance(g0) = 6
    c: Vertical(g0)
    c: Coincident(g3,g0)
    c: Weight(g1) = 1
    c: Equal(g1,g2)
    c: InternalAlignment(g1,g3)
    c: InternalAlignment(g2,g3)
    c: InternalAlignment(g4,g3)
    c: InternalAlignment(g5,g3)
    c: Block(g3)
    c: Coincident(g6,g0)
    c: Coincident(g6,g3)
    c: Horizontal(g6)
FEATURE [Part::Extrusion] Extrude017  label="caseScrewPillarBracket005"
  Base = -> Sketch023
  Dir = (0,0,1)
  DirMode = 2
  FaceMakerClass = Part::FaceMakerBullseye
  LengthFwd = 2.4
  LengthRev = 0
  Placement = pos=(90.7,29,6.77) rot=(0,-1,0;1.5708rad)
  Solid = true
  Symmetric = false
FEATURE [Sketcher::SketchObject] Sketch024
  FullyConstrained = true
  sketch-geometry (7):
    g0: LineSegment StartX=0 StartY=0 StartZ=0 EndX=0 EndY=6 EndZ=0
    g1: Circle CenterX=0 CenterY=0 CenterZ=0 NormalX=0 NormalY=0 NormalZ=1 AngleXU=0 Radius=1
    g2: Circle CenterX=8 CenterY=6 CenterZ=0 NormalX=0 NormalY=0 NormalZ=1 AngleXU=0 Radius=1
    g3: BSplineCurve PolesCount=3 KnotsCount=2 Degree=2 IsPeriodic=0
    g4: GeomPoint X=0 Y=0 Z=0
    g5: GeomPoint X=8 Y=6 Z=0
    g6: LineSegment StartX=0 StartY=6 StartZ=0 EndX=8 EndY=6 EndZ=0
  constraints (14):
    c: Coincident(g0,g-1)
    c: Distance(g0) = 6
    c: Vertical(g0)
    c: Coincident(g3,g0)
    c: Weight(g1) = 1
    c: Equal(g1,g2)
    c: InternalAlignment(g1,g3)
    c: InternalAlignment(g2,g3)
    c: InternalAlignment(g4,g3)
    c: InternalAlignment(g5,g3)
    c: Block(g3)
    c: Coincident(g6,g0)
    c: Coincident(g6,g3)
    c: Horizontal(g6)
FEATURE [Part::Extrusion] Extrude018  label="caseScrewPillarBracket006"
  Base = -> Sketch024
  Dir = (0,0,1)
  DirMode = 2
  FaceMakerClass = Part::FaceMakerBullseye
  LengthFwd = 2.4
  LengthRev = 0
  Placement = pos=(103.7,29,6.77) rot=(0,-1,0;1.5708rad)
  Solid = true
  Symmetric = false
FEATURE [Sketcher::SketchObject] Sketch025
  FullyConstrained = true
  sketch-geometry (7):
    g0: LineSegment StartX=0 StartY=0 StartZ=0 EndX=0 EndY=6 EndZ=0
    g1: Circle CenterX=0 CenterY=0 CenterZ=0 NormalX=0 NormalY=0 NormalZ=1 AngleXU=0 Radius=1
    g2: Circle CenterX=8 CenterY=6 CenterZ=0 NormalX=0 NormalY=0 NormalZ=1 AngleXU=0 Radius=1
    g3: BSplineCurve PolesCount=3 KnotsCount=2 Degree=2 IsPeriodic=0
    g4: GeomPoint X=0 Y=0 Z=0
    g5: GeomPoint X=8 Y=6 Z=0
    g6: LineSegment StartX=0 StartY=6 StartZ=0 EndX=8 EndY=6 EndZ=0
  constraints (14):
    c: Coincident(g0,g-1)
    c: Distance(g0) = 6
    c: Vertical(g0)
    c: Coincident(g3,g0)
    c: Weight(g1) = 1
    c: Equal(g1,g2)
    c: InternalAlignment(g1,g3)
    c: InternalAlignment(g2,g3)
    c: InternalAlignment(g4,g3)
    c: InternalAlignment(g5,g3)
    c: Block(g3)
    c: Coincident(g6,g0)
    c: Coincident(g6,g3)
    c: Horizontal(g6)
FEATURE [Part::Extrusion] Extrude019  label="caseScrewPillarBracket007"
  Base = -> Sketch025
  Dir = (0,0,1)
  DirMode = 2
  FaceMakerClass = Part::FaceMakerBullseye
  LengthFwd = 2.4
  LengthRev = 0
  Placement = pos=(101.3,29,65.23) rot=(0,1,0;1.5708rad)
  Solid = true
  Symmetric = false
FEATURE [Part::Box] Box011  label="frontCaseScrewPillarBracket"
  AttacherType = Attacher::AttachEngine3D
  Height = 2.4
  Length = 16
  Placement = pos=(87,28,2.3) rot=(0,0,1;0rad)
  Width = 7
FEATURE [Part::Box] Box012  label="frontCaseScrewPillarBracket001"
  AttacherType = Attacher::AttachEngine3D
  Height = 2.4
  Length = 16
  Placement = pos=(87,28,67.3) rot=(0,0,1;0rad)
  Width = 7
FEATURE [Sketcher::SketchObject] Sketch026
  FullyConstrained = true
  sketch-geometry (17):
    g0: Circle CenterX=-3.5 CenterY=23.5 CenterZ=0 NormalX=0 NormalY=0 NormalZ=1 AngleXU=0 Radius=1
    g1: Circle CenterX=-1 CenterY=15.25 CenterZ=0 NormalX=0 NormalY=0 NormalZ=1 AngleXU=0 Radius=1
    g2: Circle CenterX=-3.5 CenterY=7 CenterZ=0 NormalX=0 NormalY=0 NormalZ=1 AngleXU=0 Radius=1
    g3: BSplineCurve PolesCount=3 KnotsCount=2 Degree=2 IsPeriodic=0
    g4: GeomPoint X=-3.5 Y=23.5 Z=0
    g5: GeomPoint X=-3.5 Y=7 Z=0
    g6: Circle CenterX=-4.8 CenterY=30.5 CenterZ=0 NormalX=0 NormalY=0 NormalZ=1 AngleXU=0 Radius=1
    g7: Circle CenterX=-3.5 CenterY=30.5 CenterZ=0 NormalX=0 NormalY=0 NormalZ=1 AngleXU=0 Radius=1
    g8: Circle CenterX=-3.5 CenterY=29.2 CenterZ=0 NormalX=0 NormalY=0 NormalZ=1 AngleXU=0 Radius=1
    g9: BSplineCurve PolesCount=3 KnotsCount=2 Degree=2 IsPeriodic=0
    g10: GeomPoint X=-4.8 Y=30.5 Z=0
    g11: GeomPoint X=-3.5 Y=29.2 Z=0
    g12: LineSegment StartX=-3.5 StartY=29.2 StartZ=0 EndX=-3.5 EndY=23.5 EndZ=0
    g13: LineSegment StartX=-4.8 StartY=30.5 StartZ=0 EndX=0 EndY=30.5 EndZ=0
    g14: LineSegment StartX=-3.5 StartY=5 StartZ=0 EndX=-3.5 EndY=7 EndZ=0
    g15: LineSegment StartX=0 StartY=5 StartZ=0 EndX=0 EndY=30.5 EndZ=0
    g16: LineSegment StartX=-3.5 StartY=5 StartZ=0 EndX=0 EndY=5 EndZ=0
  constraints (33):
    c: Weight(g0) = 1
    c: Equal(g0,g1)
    c: Equal(g0,g2)
    c: InternalAlignment(g0,g3)
    c: InternalAlignment(g1,g3)
    c: InternalAlignment(g2,g3)
    c: InternalAlignment(g4,g3)
    c: InternalAlignment(g5,g3)
    c: Block(g3)
    c: Weight(g6) = 1
    c: Equal(g6,g7)
    c: Equal(g6,g8)
    c: InternalAlignment(g6,g9)
    c: InternalAlignment(g7,g9)
    c: InternalAlignment(g8,g9)
    c: InternalAlignment(g10,g9)
    c: InternalAlignment(g11,g9)
    c: Block(g9)
    c: Coincident(g12,g9)
    c: Coincident(g12,g3)
    c: Vertical(g12)
    c: Coincident(g13,g9)
    c: Horizontal(g13)
    c: Distance(g13) = 4.8
    c: Coincident(g14,g3)
    c: Vertical(g14)
    c: Coincident(g15,g13)
    c: Vertical(g15)
    c: Tangent(g15,g1)
    c: Distance(g14) = 2
    c: Coincident(g16,g14)
    c: Horizontal(g16)
    c: Coincident(g15,g16)
FEATURE [Part::Feature] Face050
  shape: bbox 4.8 x 25.5 x 2e-07 mm, 1 faces, 0 solids (baked)
FEATURE [Part::Revolution] Revolve054  label="moreFrontCaseScrewPost001"
  Angle = 360
  Axis = (0,1,0)
  Base = (0,0,0)
  FaceMakerClass = Part::FaceMakerBullseye
  Placement = pos=(102.5,4.5,3.5) rot=(0,0,1;0rad)
  Solid = false
  Source = -> Face050
  Symmetric = false
FEATURE [Part::Feature] Face051
  shape: bbox 4.8 x 25.5 x 2e-07 mm, 1 faces, 0 solids (baked)
FEATURE [Part::Revolution] Revolve055  label="moreFrontCaseScrewPost002"
  Angle = 360
  Axis = (0,1,0)
  Base = (0,0,0)
  FaceMakerClass = Part::FaceMakerBullseye
  Placement = pos=(102.5,4.5,68.5) rot=(0,0,1;0rad)
  Solid = false
  Source = -> Face051
  Symmetric = false
FEATURE [Sketcher::SketchObject] Sketch027
  FullyConstrained = true
  sketch-geometry (10):
    g0: LineSegment StartX=-1.6 StartY=4.7 StartZ=0 EndX=-1.6 EndY=1.7 EndZ=0
    g1: LineSegment StartX=-3.5 StartY=4.7 StartZ=0 EndX=-1.6 EndY=4.7 EndZ=0
    g2: LineSegment StartX=-1.6 StartY=1.7 StartZ=0 EndX=-1.6 EndY=1.5 EndZ=0
    g3: LineSegment StartX=-1.6 StartY=1.5 StartZ=0 EndX=-5.2 EndY=1.5 EndZ=0
    g4: Circle CenterX=-3.5 CenterY=4.7 CenterZ=0 NormalX=0 NormalY=0 NormalZ=1 AngleXU=0 Radius=1
    g5: Circle CenterX=-3.59627 CenterY=2.99743 CenterZ=0 NormalX=0 NormalY=0 NormalZ=1 AngleXU=0 Radius=1
    g6: Circle CenterX=-5.2 CenterY=1.5 CenterZ=0 NormalX=0 NormalY=0 NormalZ=1 AngleXU=0 Radius=1
    g7: BSplineCurve PolesCount=3 KnotsCount=2 Degree=2 IsPeriodic=0
    g8: GeomPoint X=-3.5 Y=4.7 Z=0
    g9: GeomPoint X=-5.2 Y=1.5 Z=0
  constraints (23):
    c: Vertical(g0)
    c: Distance(g0) = 3
    c: Coincident(g1,g0)
    c: Horizontal(g1)
    c: Block(g0)
    c: Block(g1)
    c: Coincident(g2,g0)
    c: Vertical(g2)
    c: Distance(g2) = 0.2
    c: Coincident(g3,g2)
    c: Horizontal(g3)
    c: Block(g3)
    c: Coincident(g7,g1)
    c: Weight(g4) = 1
    c: Equal(g4,g5)
    c: Equal(g4,g6)
    c: Coincident(g7,g3)
    c: InternalAlignment(g4,g7)
    c: InternalAlignment(g5,g7)
    c: InternalAlignment(g6,g7)
    c: InternalAlignment(g8,g7)
    c: InternalAlignment(g9,g7)
    c: Block(g7)
FEATURE [Sketcher::SketchObject] Sketch028
  FullyConstrained = true
  sketch-geometry (18):
    g0: LineSegment StartX=0 StartY=3e-16 StartZ=0 EndX=0 EndY=1.7 EndZ=0
    g1: LineSegment StartX=-3.5 StartY=0 StartZ=0 EndX=-3.5 EndY=0.9 EndZ=0
    g2: Circle CenterX=-2.7 CenterY=1.7 CenterZ=0 NormalX=0 NormalY=0 NormalZ=1 AngleXU=0 Radius=1
    g3: Circle CenterX=-3.5 CenterY=1.7 CenterZ=0 NormalX=0 NormalY=0 NormalZ=1 AngleXU=0 Radius=1
    g4: Circle CenterX=-3.5 CenterY=0.9 CenterZ=0 NormalX=0 NormalY=0 NormalZ=1 AngleXU=0 Radius=1
    g5: BSplineCurve PolesCount=3 KnotsCount=2 Degree=2 IsPeriodic=0
    g6: GeomPoint X=-2.7 Y=1.7 Z=0
    g7: GeomPoint X=-3.5 Y=0.9 Z=0
    g8: LineSegment StartX=-3.5 StartY=0 StartZ=0 EndX=-3.5 EndY=-7 EndZ=0
    g9: LineSegment StartX=0 StartY=3e-16 StartZ=0 EndX=0 EndY=-7 EndZ=0
    g10: LineSegment StartX=-3.5 StartY=-7 StartZ=0 EndX=0 EndY=-7 EndZ=0
    g11: LineSegment StartX=-2.7 StartY=1.7 StartZ=0 EndX=-1.6 EndY=1.7 EndZ=0
    g12: LineSegment StartX=0 StartY=1.7 StartZ=0 EndX=0 EndY=4.5 EndZ=0
    g13: LineSegment StartX=0 StartY=4.5 StartZ=0 EndX=0 EndY=10.8 EndZ=0
    g14: LineSegment StartX=0 StartY=10.8 StartZ=0 EndX=-2 EndY=10.8 EndZ=0
    g15: LineSegment StartX=-1.6 StartY=4.7 StartZ=0 EndX=-1.6 EndY=1.7 EndZ=0
    g16: LineSegment StartX=-1.6 StartY=4.7 StartZ=0 EndX=-2 EndY=4.7 EndZ=0
    g17: LineSegment StartX=-2 StartY=4.7 StartZ=0 EndX=-2 EndY=10.8 EndZ=0
  constraints (44):
    c: Vertical(g0)
    c: Vertical(g1)
    c: Distance(g1) = 0.9
    c: Block(g0)
    c: Distance(g0) = 1.7
    c: Weight(g2) = 1
    c: Equal(g2,g3)
    c: Equal(g2,g4)
    c: Coincident(g5,g1)
    c: InternalAlignment(g2,g5)
    c: InternalAlignment(g3,g5)
    c: InternalAlignment(g4,g5)
    c: InternalAlignment(g6,g5)
    c: InternalAlignment(g7,g5)
    c: Block(g5)
    c: Coincident(g8,g1)
    c: Vertical(g8)
    c: Distance(g8) = 7
    c: Vertical(g9)
    c: Equal(g8,g9) = 7
    c: Coincident(g9,g0)
    c: Coincident(g10,g8)
    c: Coincident(g10,g9)
    c: Horizontal(g10)
    c: Coincident(g11,g5)
    c: Horizontal(g11)
    c: Coincident(g12,g0)
    c: Vertical(g12)
    c: Distance(g12) = 2.8
    c: Coincident(g13,g12)
    c: Vertical(g13)
    c: Distance(g13) = 6.3
    c: Coincident(g14,g13)
    c: Horizontal(g14)
    c: Distance(g14) = 2
    c: Vertical(g15)
    c: Distance(g15) = 3
    c: Block(g11)
    c: Coincident(g15,g11)
    c: Coincident(g16,g15)
    c: Horizontal(g16)
    c: Coincident(g17,g16)
    c: Coincident(g17,g14)
    c: Vertical(g17)
FEATURE [Part::Revolution] Revolve040  label="backCaseScrewRetainer001"
  Angle = 360
  Axis = (0,1,0)
  Base = (0,0,0)
  FaceMakerClass = Part::FaceMakerBullseye
  Placement = pos=(12.5,3,10) rot=(0,0,1;0rad)
  Solid = false
  Source = -> Face036
  Symmetric = false
FEATURE [Part::Feature] Face055
  shape: bbox 3.5 x 30.2 x 2e-07 mm, 1 faces, 0 solids (baked)
FEATURE [Part::Revolution] Revolve059  label="backCaseScrewPost"
  Angle = 360
  Axis = (0,1,0)
  Base = (0,0,0)
  FaceMakerClass = Part::FaceMakerBullseye
  Placement = pos=(12.5,4.5,10) rot=(0,0,1;0rad)
  Solid = false
  Source = -> Face055
  Symmetric = false
FEATURE [Part::Feature] Face056
  shape: bbox 3.5 x 30.2 x 2e-07 mm, 1 faces, 0 solids (baked)
FEATURE [Part::Revolution] Revolve060  label="backCaseScrewPost001"
  Angle = 360
  Axis = (0,1,0)
  Base = (0,0,0)
  FaceMakerClass = Part::FaceMakerBullseye
  Placement = pos=(12.5,4.5,62) rot=(0,0,1;0rad)
  Solid = false
  Source = -> Face056
  Symmetric = false
FEATURE [Part::Feature] Face057
  shape: bbox 3.5 x 17.8 x 2e-07 mm, 1 faces, 0 solids (baked)
FEATURE [Part::Revolution] Revolve061  label="removeToCreateScrewAndThreadedInsertHole"
  Angle = 360
  Axis = (0,1,0)
  Base = (0,0,0)
  FaceMakerClass = Part::FaceMakerBullseye
  Placement = pos=(12.5,0,10) rot=(0,0,1;0rad)
  Solid = false
  Source = -> Face057
  Symmetric = false
FEATURE [Part::Feature] Face058
  shape: bbox 3.5 x 17.8 x 2e-07 mm, 1 faces, 0 solids (baked)
FEATURE [Part::Revolution] Revolve062  label="removeToCreateScrewAndThreadedInsertHole001"
  Angle = 360
  Axis = (0,1,0)
  Base = (0,0,0)
  FaceMakerClass = Part::FaceMakerBullseye
  Placement = pos=(12.5,0,62) rot=(0,0,1;0rad)
  Solid = false
  Source = -> Face058
  Symmetric = false
FEATURE [Part::Feature] Face059
  shape: bbox 3.5 x 17.8 x 2e-07 mm, 1 faces, 0 solids (baked)
FEATURE [Part::Revolution] Revolve063  label="removeToCreateScrewAndThreadedInsertHole002"
  Angle = 360
  Axis = (0,1,0)
  Base = (0,0,0)
  FaceMakerClass = Part::FaceMakerBullseye
  Placement = pos=(89.5,0,68.5) rot=(0,0,1;0rad)
  Solid = false
  Source = -> Face059
  Symmetric = false
FEATURE [Part::Feature] Face060
  shape: bbox 3.5 x 17.8 x 2e-07 mm, 1 faces, 0 solids (baked)
FEATURE [Part::Revolution] Revolve064  label="removeToCreateScrewAndThreadedInsertHole003"
  Angle = 360
  Axis = (0,1,0)
  Base = (0,0,0)
  FaceMakerClass = Part::FaceMakerBullseye
  Placement = pos=(89.5,0,3.5) rot=(0,0,1;0rad)
  Solid = false
  Source = -> Face060
  Symmetric = false
FEATURE [Part::Feature] Face061
  shape: bbox 3.5 x 17.8 x 2e-07 mm, 1 faces, 0 solids (baked)
FEATURE [Part::Revolution] Revolve065  label="removeToCreateScrewAndThreadedInsertHole004"
  Angle = 360
  Axis = (0,1,0)
  Base = (0,0,0)
  FaceMakerClass = Part::FaceMakerBullseye
  Placement = pos=(102.5,4.7,3.5) rot=(0,0,1;0rad)
  Solid = false
  Source = -> Face061
  Symmetric = false
FEATURE [Part::Feature] Face062
  shape: bbox 3.5 x 17.8 x 2e-07 mm, 1 faces, 0 solids (baked)
FEATURE [Part::Revolution] Revolve066  label="removeToCreateScrewAndThreadedInsertHole005"
  Angle = 360
  Axis = (0,1,0)
  Base = (0,0,0)
  FaceMakerClass = Part::FaceMakerBullseye
  Placement = pos=(102.5,4.7,68.5) rot=(0,0,1;0rad)
  Solid = false
  Source = -> Face062
  Symmetric = false
FEATURE [Part::MultiFuse] Fusion047  label="makeHoles"
  Shapes = -> [Revolve066,Revolve065,Revolve064,Revolve063,Revolve062,Revolve061]
FEATURE [Part::Feature] Face063
  shape: bbox 3.6 x 3.2 x 2e-07 mm, 1 faces, 0 solids (baked)
FEATURE [Part::Revolution] Revolve067  label="moreFrontCaseScrewRetainer002"
  Angle = 360
  Axis = (0,1,0)
  Base = (0,0,0)
  FaceMakerClass = Part::FaceMakerBullseye
  Placement = pos=(102.5,4.5,68.5) rot=(0,0,1;0rad)
  Solid = false
  Source = -> Face063
  Symmetric = false
FEATURE [Part::Feature] Face064
  shape: bbox 3.6 x 3.2 x 2e-07 mm, 1 faces, 0 solids (baked)
FEATURE [Part::Revolution] Revolve068  label="moreFrontCaseScrewRetainer003"
  Angle = 360
  Axis = (0,1,0)
  Base = (0,0,0)
  FaceMakerClass = Part::FaceMakerBullseye
  Placement = pos=(102.5,4.5,3.5) rot=(0,0,1;0rad)
  Solid = false
  Source = -> Face064
  Symmetric = false
FEATURE [Part::Feature] Face065
  shape: bbox 3.5 x 17.8 x 2e-07 mm, 1 faces, 0 solids (baked)
FEATURE [Part::Revolution] Revolve069  label="removeToCreateScrewAndThreadedInsertHole006"
  Angle = 360
  Axis = (0,1,0)
  Base = (0,0,0)
  FaceMakerClass = Part::FaceMakerBullseye
  Placement = pos=(12.5,0,10) rot=(0,0,1;0rad)
  Solid = false
  Source = -> Face065
  Symmetric = false
FEATURE [Part::Feature] Face066
  shape: bbox 3.5 x 17.8 x 2e-07 mm, 1 faces, 0 solids (baked)
FEATURE [Part::Revolution] Revolve070  label="removeToCreateScrewAndThreadedInsertHole007"
  Angle = 360
  Axis = (0,1,0)
  Base = (0,0,0)
  FaceMakerClass = Part::FaceMakerBullseye
  Placement = pos=(12.5,0,62) rot=(0,0,1;0rad)
  Solid = false
  Source = -> Face066
  Symmetric = false
FEATURE [Part::Feature] Face067
  shape: bbox 3.5 x 17.8 x 2e-07 mm, 1 faces, 0 solids (baked)
FEATURE [Part::Revolution] Revolve071  label="removeToCreateScrewAndThreadedInsertHole008"
  Angle = 360
  Axis = (0,1,0)
  Base = (0,0,0)
  FaceMakerClass = Part::FaceMakerBullseye
  Placement = pos=(89.5,0,68.5) rot=(0,0,1;0rad)
  Solid = false
  Source = -> Face067
  Symmetric = false
FEATURE [Part::Feature] Face068
  shape: bbox 3.5 x 17.8 x 2e-07 mm, 1 faces, 0 solids (baked)
FEATURE [Part::Revolution] Revolve072  label="removeToCreateScrewAndThreadedInsertHole009"
  Angle = 360
  Axis = (0,1,0)
  Base = (0,0,0)
  FaceMakerClass = Part::FaceMakerBullseye
  Placement = pos=(89.5,0,3.5) rot=(0,0,1;0rad)
  Solid = false
  Source = -> Face068
  Symmetric = false
FEATURE [Part::Feature] Face069
  shape: bbox 3.5 x 17.8 x 2e-07 mm, 1 faces, 0 solids (baked)
FEATURE [Part::Feature] Face070
  shape: bbox 3.5 x 17.8 x 2e-07 mm, 1 faces, 0 solids (baked)
FEATURE [Part::Revolution] Revolve073  label="removeToCreateScrewAndThreadedInsertHole010"
  Angle = 360
  Axis = (0,1,0)
  Base = (0,0,0)
  FaceMakerClass = Part::FaceMakerBullseye
  Placement = pos=(102.5,4.7,3.5) rot=(0,0,1;0rad)
  Solid = false
  Source = -> Face069
  Symmetric = false
FEATURE [Part::Revolution] Revolve074  label="removeToCreateScrewAndThreadedInsertHole011"
  Angle = 360
  Axis = (0,1,0)
  Base = (0,0,0)
  FaceMakerClass = Part::FaceMakerBullseye
  Placement = pos=(102.5,4.7,68.5) rot=(0,0,1;0rad)
  Solid = false
  Source = -> Face070
  Symmetric = false
FEATURE [Part::MultiFuse] Fusion048  label="makeHoles001"
  Shapes = -> [Revolve074,Revolve073,Revolve072,Revolve071,Revolve070,Revolve069]
FEATURE [Part::MultiFuse] Fusion049  label="caseScrewRetainers"
  Shapes = -> [Revolve067,Revolve068,Revolve048,Revolve047,Revolve039,Revolve040]
FEATURE [Part::Cut] Cut015  label="caseScrewRetainers001"
  Base = -> Fusion049
  Tool = -> Fusion048
FEATURE [Part::MultiFuse] Fusion050  label="casePillars"
  Shapes = -> [Revolve055,Revolve054,Revolve043,Revolve046,Revolve059,Revolve060]
FEATURE [Part::Feature] Face071 .. Face076  x6 (patterned run collapsed; names and placements below)
  shape: bbox 3.5 x 17.8 x 2e-07 mm, 1 faces, 0 solids (baked)
FEATURE [Part::Revolution] Revolve075  label="removeToCreateScrewAndThreadedInsertHole012"
  Angle = 360
  Axis = (0,1,0)
  Base = (0,0,0)
  FaceMakerClass = Part::FaceMakerBullseye
  Placement = pos=(12.5,0,10) rot=(0,0,1;0rad)
  Solid = false
  Source = -> Face071
  Symmetric = false
FEATURE [Part::Revolution] Revolve076  label="removeToCreateScrewAndThreadedInsertHole013"
  Angle = 360
  Axis = (0,1,0)
  Base = (0,0,0)
  FaceMakerClass = Part::FaceMakerBullseye
  Placement = pos=(12.5,0,62) rot=(0,0,1;0rad)
  Solid = false
  Source = -> Face072
  Symmetric = false
FEATURE [Part::Revolution] Revolve077  label="removeToCreateScrewAndThreadedInsertHole014"
  Angle = 360
  Axis = (0,1,0)
  Base = (0,0,0)
  FaceMakerClass = Part::FaceMakerBullseye
  Placement = pos=(89.5,0,68.5) rot=(0,0,1;0rad)
  Solid = false
  Source = -> Face073
  Symmetric = false
FEATURE [Part::Revolution] Revolve078  label="removeToCreateScrewAndThreadedInsertHole015"
  Angle = 360
  Axis = (0,1,0)
  Base = (0,0,0)
  FaceMakerClass = Part::FaceMakerBullseye
  Placement = pos=(89.5,0,3.5) rot=(0,0,1;0rad)
  Solid = false
  Source = -> Face074
  Symmetric = false
FEATURE [Part::Revolution] Revolve079  label="removeToCreateScrewAndThreadedInsertHole016"
  Angle = 360
  Axis = (0,1,0)
  Base = (0,0,0)
  FaceMakerClass = Part::FaceMakerBullseye
  Placement = pos=(102.5,4.7,3.5) rot=(0,0,1;0rad)
  Solid = false
  Source = -> Face075
  Symmetric = false
FEATURE [Part::Revolution] Revolve080  label="removeToCreateScrewAndThreadedInsertHole017"
  Angle = 360
  Axis = (0,1,0)
  Base = (0,0,0)
  FaceMakerClass = Part::FaceMakerBullseye
  Placement = pos=(102.5,4.7,68.5) rot=(0,0,1;0rad)
  Solid = false
  Source = -> Face076
  Symmetric = false
FEATURE [Part::MultiFuse] Fusion051  label="makeHoles002"
  Shapes = -> [Revolve080,Revolve079,Revolve078,Revolve077,Revolve076,Revolve075]
FEATURE [Part::Cut] Cut016  label="caesPillars"
  Base = -> Fusion050
  Tool = -> Fusion051
FEATURE [Part::Revolution] Revolve009  label="plugHousing016"
  Angle = 360
  Axis = (0,1,0)
  Base = (0,0,0)
  FaceMakerClass = Part::FaceMakerBullseye
  Placement = pos=(0,0,36.15) rot=(0,0,1;0rad)
  Solid = false
  Source = -> Face012
  Symmetric = false
FEATURE [Part::MultiFuse] Fusion014  label="plugHousing023"
  Placement = pos=(0,0,0) rot=(0,0,1;1.5708rad)
  Shapes = -> [Revolve011,Revolve009]
FEATURE [Part::Revolution] Revolve010  label="plugHousing017"
  Angle = 360
  Axis = (0,1,0)
  Base = (0,0,0)
  FaceMakerClass = Part::FaceMakerBullseye
  Placement = pos=(0,0,36.15) rot=(0,0,1;0rad)
  Solid = false
  Source = -> Face014
  Symmetric = false
FEATURE [Part::MultiFuse] Fusion015  label="plugHousing024"
  Placement = pos=(0,0,0) rot=(0,0,1;1.5708rad)
  Shapes = -> [Revolve010,Revolve015]
FEATURE [Part::Revolution] Revolve014  label="plugHousing026"
  Angle = 360
  Axis = (0,1,0)
  Base = (0,0,0)
  FaceMakerClass = Part::FaceMakerBullseye
  Placement = pos=(0,0,36.15) rot=(0,0,1;0rad)
  Solid = false
  Source = -> Face011
  Symmetric = false
FEATURE [Part::Revolution] Revolve013  label="plugHousing025"
  Angle = 360
  Axis = (0,1,0)
  Base = (0,0,0)
  FaceMakerClass = Part::FaceMakerBullseye
  Placement = pos=(0,0,36.15) rot=(0,0,1;0rad)
  Solid = false
  Source = -> Face015
  Symmetric = false
FEATURE [Part::MultiFuse] Fusion016  label="plugHousing028"
  Placement = pos=(0,19,0) rot=(0,0,1;3.14159rad)
  Shapes = -> [Fusion014,Fusion013]
FEATURE [Part::MultiFuse] Fusion011  label="plugHousing018"
  Placement = pos=(0,0,0) rot=(0,0,1;1.5708rad)
  Shapes = -> [Revolve014,Revolve013]
FEATURE [Part::MultiFuse] Fusion012  label="plugHousing019"
  Placement = pos=(0,19,0) rot=(0,0,1;3.14159rad)
  Shapes = -> [Fusion011,Fusion015]
FEATURE [Part::MultiFuse] Fusion017  label="plugHousing029"
  Placement = pos=(122.621,0,-0.15) rot=(0,0,1;0rad)
  Shapes = -> [Fusion016,Fusion012]
FEATURE [Part::MultiFuse] Fusion052  label="casePillarRetainers"
  Shapes = -> [Extrude012,Extrude013,Extrude014,Extrude015,Extrude016,Extrude017,Extrude018,Extrude019,Box011,Box012]
FEATURE [Part::Feature] Face077
  shape: bbox 3.5 x 17.8 x 2e-07 mm, 1 faces, 0 solids (baked)
FEATURE [Part::Revolution] Revolve081  label="removeToCreateScrewAndThreadedInsertHole018"
  Angle = 360
  Axis = (0,1,0)
  Base = (0,0,0)
  FaceMakerClass = Part::FaceMakerBullseye
  Placement = pos=(62.3,30.3,19.7) rot=(0,0,1;0rad)
  Solid = false
  Source = -> Face077
  Symmetric = false
FEATURE [Part::Feature] Face078
  shape: bbox 3.5 x 17.8 x 2e-07 mm, 1 faces, 0 solids (baked)
FEATURE [Part::Revolution] Revolve082  label="removeToCreateScrewAndThreadedInsertHole019"
  Angle = 360
  Axis = (0,1,0)
  Base = (0,0,0)
  FaceMakerClass = Part::FaceMakerBullseye
  Placement = pos=(62.3,30.3,51.7) rot=(0,0,1;0rad)
  Solid = false
  Source = -> Face078
  Symmetric = false
FEATURE [Part::Feature] Face079
  shape: bbox 3.5 x 17.8 x 2e-07 mm, 1 faces, 0 solids (baked)
FEATURE [Part::Revolution] Revolve083  label="removeToCreateScrewAndThreadedInsertHole020"
  Angle = 360
  Axis = (0,1,0)
  Base = (0,0,0)
  FaceMakerClass = Part::FaceMakerBullseye
  Placement = pos=(30.3,30.3,19.7) rot=(0,0,1;0rad)
  Solid = false
  Source = -> Face079
  Symmetric = false
FEATURE [Part::Feature] Face080
  shape: bbox 3.5 x 17.8 x 2e-07 mm, 1 faces, 0 solids (baked)
FEATURE [Part::Revolution] Revolve084  label="removeToCreateScrewAndThreadedInsertHole021"
  Angle = 360
  Axis = (0,1,0)
  Base = (0,0,0)
  FaceMakerClass = Part::FaceMakerBullseye
  Placement = pos=(30.3,30.3,51.7) rot=(0,0,1;0rad)
  Solid = false
  Source = -> Face080
  Symmetric = false
FEATURE [Part::MultiFuse] Fusion053  label="createThreadedInsertHolesForFan"
  Shapes = -> [Revolve081,Revolve082,Revolve083,Revolve084]
FEATURE [Part::Cut] Cut017  label="fanScrewHousing001"
  Base = -> Fusion046
  Tool = -> Fusion053
FEATURE [Part::Feature] Face081
  shape: bbox 3.5 x 17.8 x 2e-07 mm, 1 faces, 0 solids (baked)
FEATURE [Part::Revolution] Revolve085  label="removeToCreateScrewAndThreadedInsertHole022"
  Angle = 360
  Axis = (0,1,0)
  Base = (0,0,0)
  FaceMakerClass = Part::FaceMakerBullseye
  Placement = pos=(62.3,30.3,19.7) rot=(0,0,1;0rad)
  Solid = false
  Source = -> Face081
  Symmetric = false
FEATURE [Part::Feature] Face082
  shape: bbox 3.5 x 17.8 x 2e-07 mm, 1 faces, 0 solids (baked)
FEATURE [Part::Revolution] Revolve086  label="removeToCreateScrewAndThreadedInsertHole023"
  Angle = 360
  Axis = (0,1,0)
  Base = (0,0,0)
  FaceMakerClass = Part::FaceMakerBullseye
  Placement = pos=(62.3,30.3,51.7) rot=(0,0,1;0rad)
  Solid = false
  Source = -> Face082
  Symmetric = false
FEATURE [Part::Feature] Face083
  shape: bbox 3.5 x 17.8 x 2e-07 mm, 1 faces, 0 solids (baked)
FEATURE [Part::Revolution] Revolve087  label="removeToCreateScrewAndThreadedInsertHole024"
  Angle = 360
  Axis = (0,1,0)
  Base = (0,0,0)
  FaceMakerClass = Part::FaceMakerBullseye
  Placement = pos=(30.3,30.3,19.7) rot=(0,0,1;0rad)
  Solid = false
  Source = -> Face083
  Symmetric = false
FEATURE [Part::Feature] Face084
  shape: bbox 3.5 x 17.8 x 2e-07 mm, 1 faces, 0 solids (baked)
FEATURE [Part::Revolution] Revolve088  label="removeToCreateScrewAndThreadedInsertHole025"
  Angle = 360
  Axis = (0,1,0)
  Base = (0,0,0)
  FaceMakerClass = Part::FaceMakerBullseye
  Placement = pos=(30.3,30.3,51.7) rot=(0,0,1;0rad)
  Solid = false
  Source = -> Face084
  Symmetric = false
FEATURE [Part::MultiFuse] Fusion054  label="createThreadedInsertHolesForFan001"
  Shapes = -> [Revolve085,Revolve086,Revolve087,Revolve088]
FEATURE [Part::Cut] Cut018  label="top007"
  Base = -> Fusion040
  Tool = -> Fusion054
FEATURE [Sketcher::SketchObject] Sketch029
  FullyConstrained = false
  Placement = pos=(0,0,0) rot=(1,0,0;1.5708rad)
  sketch-geometry (24):
    g0: ArcOfCircle CenterX=-4 CenterY=-10.5 CenterZ=0 NormalX=0 NormalY=0 NormalZ=1 AngleXU=0 Radius=1.5 StartAngle=6e-16 EndAngle=3.14159
    g1: ArcOfCircle CenterX=-34.2 CenterY=-10.5 CenterZ=0 NormalX=0 NormalY=0 NormalZ=1 AngleXU=0 Radius=1.5 StartAngle=0 EndAngle=3.14159
    g2: ArcOfCircle CenterX=-34.2 CenterY=-27.7 CenterZ=0 NormalX=0 NormalY=0 NormalZ=1 AngleXU=0 Radius=1.5 StartAngle=3.14159 EndAngle=6.28319
    g3: ArcOfCircle CenterX=-4 CenterY=-27.7 CenterZ=0 NormalX=0 NormalY=0 NormalZ=1 AngleXU=0 Radius=1.5 StartAngle=3.1416 EndAngle=6.28319
    g4: ArcOfCircle CenterX=-10 CenterY=-4.3 CenterZ=0 NormalX=0 NormalY=0 NormalZ=1 AngleXU=0 Radius=1.5 StartAngle=2e-16 EndAngle=3.14159
    g5: ArcOfCircle CenterX=-16.1 CenterY=-1.8 CenterZ=0 NormalX=0 NormalY=0 NormalZ=1 AngleXU=0 Radius=1.5 StartAngle=5e-16 EndAngle=3.14159
    g6: ArcOfCircle CenterX=-22.1 CenterY=-1.8 CenterZ=0 NormalX=0 NormalY=0 NormalZ=1 AngleXU=0 Radius=1.5 StartAngle=5e-16 EndAngle=3.14159
    g7: ArcOfCircle CenterX=-28.2 CenterY=-4.3 CenterZ=0 NormalX=0 NormalY=0 NormalZ=1 AngleXU=0 Radius=1.5 StartAngle=2e-16 EndAngle=3.14159
    g8: ArcOfCircle CenterX=-10 CenterY=-33.9 CenterZ=0 NormalX=0 NormalY=0 NormalZ=1 AngleXU=0 Radius=1.5 StartAngle=3.14159 EndAngle=6.28319
    g9: ArcOfCircle CenterX=-16.1 CenterY=-36.4 CenterZ=0 NormalX=0 NormalY=0 NormalZ=1 AngleXU=0 Radius=1.5 StartAngle=3.14159 EndAngle=6.28319
    g10: ArcOfCircle CenterX=-22.1 CenterY=-36.4 CenterZ=0 NormalX=0 NormalY=0 NormalZ=1 AngleXU=0 Radius=1.5 StartAngle=3.14159 EndAngle=6.28319
    g11: ArcOfCircle CenterX=-28.2 CenterY=-33.9 CenterZ=0 NormalX=0 NormalY=0 NormalZ=1 AngleXU=0 Radius=1.5 StartAngle=3.14159 EndAngle=6.28319
    g12: LineSegment StartX=-35.7 StartY=-10.5 StartZ=0 EndX=-35.7 EndY=-27.7 EndZ=0
    g13: LineSegment StartX=-32.7 StartY=-10.5 StartZ=0 EndX=-32.7 EndY=-27.7 EndZ=0
    g14: LineSegment StartX=-29.7 StartY=-33.9 StartZ=0 EndX=-29.7 EndY=-4.3 EndZ=0
    g15: LineSegment StartX=-26.7 StartY=-33.9 StartZ=0 EndX=-26.7 EndY=-4.3 EndZ=0
    g16: LineSegment StartX=-2.5 StartY=-10.5 StartZ=0 EndX=-2.5 EndY=-27.7 EndZ=0
    g17: LineSegment StartX=-8.5 StartY=-4.3 StartZ=0 EndX=-8.5 EndY=-33.9 EndZ=0
    g18: LineSegment StartX=-5.5 StartY=-10.5 StartZ=0 EndX=-5.5 EndY=-27.7 EndZ=0
    g19: LineSegment StartX=-11.5 StartY=-4.3 StartZ=0 EndX=-11.5 EndY=-33.9 EndZ=0
    g20: LineSegment StartX=-14.6 StartY=-1.8 StartZ=0 EndX=-14.6 EndY=-36.4 EndZ=0
    g21: LineSegment StartX=-17.6 StartY=-1.8 StartZ=0 EndX=-17.6 EndY=-36.4 EndZ=0
    g22: LineSegment StartX=-20.6 StartY=-36.4 StartZ=0 EndX=-20.6 EndY=-1.8 EndZ=0
    g23: LineSegment StartX=-23.6 StartY=-1.8 StartZ=0 EndX=-23.6 EndY=-36.4 EndZ=0
  constraints (48):
    c: Block(g0)
    c: Block(g1)
    c: Block(g2)
    c: Block(g3)
    c: Block(g4)
    c: Block(g5)
    c: Block(g6)
    c: Block(g7)
    c: Block(g8)
    c: Block(g9)
    c: Block(g10)
    c: Block(g11)
    c: Coincident(g12,g1)
    c: Coincident(g12,g2)
    c: Vertical(g12)
    c: Coincident(g13,g1)
    c: Coincident(g13,g2)
    c: Vertical(g13)
    c: Coincident(g14,g11)
    c: Coincident(g14,g7)
    c: Vertical(g14)
    c: Coincident(g15,g11)
    c: Coincident(g15,g7)
    c: Vertical(g15)
    c: Coincident(g16,g0)
    c: Coincident(g16,g3)
    c: Vertical(g16)
    c: Coincident(g17,g4)
    c: Coincident(g17,g8)
    c: Vertical(g17)
    c: Coincident(g18,g0)
    c: Coincident(g18,g3)
    c: Vertical(g18)
    c: Coincident(g19,g4)
    c: Coincident(g19,g8)
    c: Vertical(g19)
    c: Coincident(g20,g5)
    c: Coincident(g20,g9)
    c: Vertical(g20)
    c: Coincident(g21,g5)
    c: Coincident(g21,g9)
    c: Vertical(g21)
    c: Coincident(g22,g10)
    c: Coincident(g22,g6)
    c: Vertical(g22)
    c: Coincident(g23,g6)
    c: Coincident(g23,g10)
    c: Vertical(g23)
FEATURE [Part::Extrusion] Extrude020  label="removeToCreateFanGrillHoles"
  Base = -> Sketch029
  Dir = (0,-1,6e-16)
  DirMode = 2
  FaceMakerClass = Part::FaceMakerBullseye
  LengthFwd = 10
  LengthRev = 0
  Placement = pos=(65.4,44,54.82) rot=(0,0,1;0rad)
  Solid = true
  Symmetric = false
FEATURE [Part::MultiFuse] Fusion055  label="top008"
  Shapes = -> [Cut017,Cut018]
FEATURE [Part::Cut] Cut019  label="top009"
  Base = -> Fusion055
  Tool = -> Extrude020
FEATURE [App::MeasureDistance] Distance003  label="Distance: 71.95 mm"
  Distance = 71.9513
  P1 = (117,38,72)
  P2 = (117,38,0.0487319)
FEATURE [Sketcher::SketchObject] Sketch030
  FullyConstrained = true
  Placement = pos=(117,19,0) rot=(0.57735,0.57735,0.57735;2.0944rad)
  sketch-geometry (48):
    g0: LineSegment StartX=-49.19 StartY=69.25 StartZ=0 EndX=-49.19 EndY=66.25 EndZ=0
    g1: LineSegment StartX=-49.19 StartY=63.5 StartZ=0 EndX=-49.19 EndY=60.5 EndZ=0
    g2: LineSegment StartX=-49.19 StartY=57.75 StartZ=0 EndX=-49.19 EndY=54.75 EndZ=0
    g3: LineSegment StartX=-49.19 StartY=52 StartZ=0 EndX=-49.19 EndY=49 EndZ=0
    g4: LineSegment StartX=-49.19 StartY=46.25 StartZ=0 EndX=-49.19 EndY=43.25 EndZ=0
    g5: LineSegment StartX=-49.19 StartY=40.5 StartZ=0 EndX=-49.19 EndY=37.5 EndZ=0
    g6: LineSegment StartX=-49.19 StartY=34.5 StartZ=0 EndX=-49.19 EndY=31.5 EndZ=0
    g7: LineSegment StartX=-49.19 StartY=28.75 StartZ=0 EndX=-49.19 EndY=25.75 EndZ=0
    g8: LineSegment StartX=-49.19 StartY=23 StartZ=0 EndX=-49.19 EndY=20 EndZ=0
    g9: LineSegment StartX=-49.19 StartY=17.25 StartZ=0 EndX=-49.19 EndY=14.25 EndZ=0
    g10: LineSegment StartX=-49.19 StartY=11.5 StartZ=0 EndX=-49.19 EndY=8.5 EndZ=0
    g11: LineSegment StartX=-49.19 StartY=5.75 StartZ=0 EndX=-49.19 EndY=2.75 EndZ=0
    g12: ArcOfCircle CenterX=-1.5 CenterY=67.75 CenterZ=0 NormalX=0 NormalY=0 NormalZ=1 AngleXU=0 Radius=1.5 StartAngle=4.71239 EndAngle=7.85398
    g13: ArcOfCircle CenterX=-1.5 CenterY=62 CenterZ=0 NormalX=0 NormalY=0 NormalZ=1 AngleXU=0 Radius=1.5 StartAngle=4.71239 EndAngle=7.85398
    g14: ArcOfCircle CenterX=-1.5 CenterY=56.25 CenterZ=0 NormalX=0 NormalY=0 NormalZ=1 AngleXU=0 Radius=1.5 StartAngle=4.71239 EndAngle=7.85398
    g15: ArcOfCircle CenterX=-11.49 CenterY=50.5 CenterZ=0 NormalX=0 NormalY=0 NormalZ=1 AngleXU=0 Radius=1.5 StartAngle=4.71239 EndAngle=7.85398
    g16: ArcOfCircle CenterX=-16.28 CenterY=44.75 CenterZ=0 NormalX=0 NormalY=0 NormalZ=1 AngleXU=0 Radius=1.5 StartAngle=4.71239 EndAngle=7.85398
    g17: ArcOfCircle CenterX=-18.2337 CenterY=39 CenterZ=0 NormalX=0 NormalY=0 NormalZ=1 AngleXU=0 Radius=1.5 StartAngle=4.71485 EndAngle=7.85398
    g18: ArcOfCircle CenterX=-16.2837 CenterY=27.25 CenterZ=0 NormalX=0 NormalY=0 NormalZ=1 AngleXU=0 Radius=1.5 StartAngle=4.71485 EndAngle=7.85398
    g19: ArcOfCircle CenterX=-18.2337 CenterY=33 CenterZ=0 NormalX=0 NormalY=0 NormalZ=1 AngleXU=0 Radius=1.5 StartAngle=4.71485 EndAngle=7.85398
    g20: ArcOfCircle CenterX=-11.49 CenterY=21.5 CenterZ=0 NormalX=0 NormalY=0 NormalZ=1 AngleXU=0 Radius=1.5 StartAngle=4.71239 EndAngle=7.85398
    g21: ArcOfCircle CenterX=-1.5 CenterY=4.25 CenterZ=0 NormalX=0 NormalY=0 NormalZ=1 AngleXU=0 Radius=1.5 StartAngle=4.71239 EndAngle=7.85398
    g22: ArcOfCircle CenterX=-1.5 CenterY=10 CenterZ=0 NormalX=0 NormalY=0 NormalZ=1 AngleXU=0 Radius=1.5 StartAngle=4.71239 EndAngle=7.85398
    g23: ArcOfCircle CenterX=-1.5 CenterY=15.75 CenterZ=0 NormalX=0 NormalY=0 NormalZ=1 AngleXU=0 Radius=1.5 StartAngle=4.71239 EndAngle=7.85398
    g24: LineSegment StartX=-49.19 StartY=69.25 StartZ=0 EndX=-1.5 EndY=69.25 EndZ=0
    g25: LineSegment StartX=-49.19 StartY=66.25 StartZ=0 EndX=-1.5 EndY=66.25 EndZ=0
    g26: LineSegment StartX=-49.19 StartY=63.5 StartZ=0 EndX=-1.5 EndY=63.5 EndZ=0
    g27: LineSegment StartX=-49.19 StartY=60.5 StartZ=0 EndX=-1.5 EndY=60.5 EndZ=0
    g28: LineSegment StartX=-49.19 StartY=57.75 StartZ=0 EndX=-1.5 EndY=57.75 EndZ=0
    g29: LineSegment StartX=-49.19 StartY=54.75 StartZ=0 EndX=-1.5 EndY=54.75 EndZ=0
    g30: LineSegment StartX=-49.19 StartY=52 StartZ=0 EndX=-11.49 EndY=52 EndZ=0
    g31: LineSegment StartX=-49.19 StartY=49 StartZ=0 EndX=-11.49 EndY=49 EndZ=0
    g32: LineSegment StartX=-49.19 StartY=46.25 StartZ=0 EndX=-16.28 EndY=46.25 EndZ=0
    g33: LineSegment StartX=-49.19 StartY=43.25 StartZ=0 EndX=-16.28 EndY=43.25 EndZ=0
    g34: LineSegment StartX=-49.19 StartY=40.5 StartZ=0 EndX=-18.2337 EndY=40.5 EndZ=0
    g35: LineSegment StartX=-49.19 StartY=37.5 StartZ=0 EndX=-18.23 EndY=37.5 EndZ=0
    g36: LineSegment StartX=-49.19 StartY=34.5 StartZ=0 EndX=-18.2337 EndY=34.5 EndZ=0
    g37: LineSegment StartX=-49.19 StartY=31.5 StartZ=0 EndX=-18.23 EndY=31.5 EndZ=0
    g38: LineSegment StartX=-49.19 StartY=28.75 StartZ=0 EndX=-16.2837 EndY=28.75 EndZ=0
    g39: LineSegment StartX=-49.19 StartY=25.75 StartZ=0 EndX=-16.28 EndY=25.75 EndZ=0
    g40: LineSegment StartX=-49.19 StartY=23 StartZ=0 EndX=-11.49 EndY=23 EndZ=0
    g41: LineSegment StartX=-49.19 StartY=20 StartZ=0 EndX=-11.49 EndY=20 EndZ=0
    g42: LineSegment StartX=-49.19 StartY=17.25 StartZ=0 EndX=-1.5 EndY=17.25 EndZ=0
    g43: LineSegment StartX=-49.19 StartY=14.25 StartZ=0 EndX=-1.5 EndY=14.25 EndZ=0
    g44: LineSegment StartX=-49.19 StartY=11.5 StartZ=0 EndX=-1.5 EndY=11.5 EndZ=0
    g45: LineSegment StartX=-49.19 StartY=8.5 StartZ=0 EndX=-1.5 EndY=8.5 EndZ=0
    g46: LineSegment StartX=-49.19 StartY=5.75 StartZ=0 EndX=-1.5 EndY=5.75 EndZ=0
    g47: LineSegment StartX=-49.19 StartY=2.75 StartZ=0 EndX=-1.5 EndY=2.75 EndZ=0
  constraints (120):
    c: Vertical(g0)
    c: Distance(g0) = 3
    c: Block(g0)
    c: Vertical(g1)
    c: Distance(g1) = 3
    c: Vertical(g2)
    c: Equal(g0,g2) = 3
    c: Block(g2)
    c: Vertical(g3)
    c: Equal(g1,g3) = 3
    c: Vertical(g4)
    c: Equal(g0,g4) = 3
    c: Block(g4)
    c: Vertical(g5)
    c: Equal(g1,g5) = 3
    c: Vertical(g6)
    c: Equal(g0,g6) = 3
    c: Block(g6)
    c: Vertical(g7)
    c: Equal(g1,g7) = 3
    c: Vertical(g8)
    c: Equal(g0,g8) = 3
    c: Block(g8)
    c: Vertical(g9)
    c: Equal(g1,g9) = 3
    c: Vertical(g10)
    c: Equal(g0,g10) = 3
    c: Block(g10)
    c: Vertical(g11)
    c: Equal(g1,g11) = 3
    c: Block(g12)
    c: Block(g13)
    c: Block(g14)
    c: Block(g15)
    c: Block(g16)
    c: Block(g17)
    c: Block(g18)
    c: Block(g19)
    c: Block(g20)
    c: Block(g21)
    c: Block(g22)
    c: Block(g23)
    c: Block(g11)
    c: Block(g9)
    c: Block(g7)
    c: Block(g5)
    c: Block(g3)
    c: Block(g1)
    c: Coincident(g24,g0)
    c: Coincident(g24,g12)
    c: Horizontal(g24)
    c: Coincident(g25,g0)
    c: Coincident(g25,g12)
    c: Horizontal(g25)
    c: Coincident(g26,g1)
    c: Coincident(g26,g13)
    c: Horizontal(g26)
    c: Coincident(g27,g1)
    c: Coincident(g27,g13)
    c: Horizontal(g27)
    c: Coincident(g28,g2)
    c: Coincident(g28,g14)
    c: Horizontal(g28)
    c: Coincident(g29,g2)
    c: Coincident(g29,g14)
    c: Horizontal(g29)
    c: Coincident(g30,g3)
    c: Coincident(g30,g15)
    c: Horizontal(g30)
    c: Coincident(g31,g3)
    c: Coincident(g31,g15)
    c: Horizontal(g31)
    c: Coincident(g32,g4)
    c: Coincident(g32,g16)
    c: Horizontal(g32)
    c: Coincident(g33,g4)
    c: Coincident(g33,g16)
    c: Horizontal(g33)
    c: Coincident(g34,g5)
    c: Coincident(g34,g17)
    c: Horizontal(g34)
    c: Coincident(g35,g5)
    c: Coincident(g35,g17)
    c: Horizontal(g35)
    c: Coincident(g36,g6)
    c: Coincident(g36,g19)
    c: Horizontal(g36)
    c: Coincident(g37,g6)
    c: Coincident(g37,g19)
    c: Horizontal(g37)
    c: Coincident(g38,g7)
    c: Coincident(g38,g18)
    c: Horizontal(g38)
    c: Coincident(g39,g7)
    c: Coincident(g39,g18)
    c: Horizontal(g39)
    c: Coincident(g40,g8)
    c: Coincident(g40,g20)
    c: Horizontal(g40)
    c: Coincident(g41,g8)
    c: Coincident(g41,g20)
    c: Horizontal(g41)
    c: Coincident(g42,g9)
    c: Coincident(g42,g23)
    c: Horizontal(g42)
    c: Coincident(g43,g9)
    c: Coincident(g43,g23)
    c: Horizontal(g43)
    c: Coincident(g44,g10)
    c: Coincident(g44,g22)
    c: Horizontal(g44)
    c: Coincident(g45,g10)
    c: Coincident(g45,g22)
    c: Horizontal(g45)
    c: Coincident(g46,g11)
    c: Coincident(g46,g21)
    c: Horizontal(g46)
    c: Coincident(g47,g11)
    c: Coincident(g47,g21)
    c: Horizontal(g47)
FEATURE [Sketcher::SketchObject] Sketch031
  FullyConstrained = true
  Placement = pos=(117,19,0) rot=(0.57735,0.57735,0.57735;2.0944rad)
  sketch-geometry (24):
    g0: ArcOfCircle CenterX=-49.19 CenterY=67.75 CenterZ=0 NormalX=0 NormalY=0 NormalZ=1 AngleXU=0 Radius=1.5 StartAngle=1.5708 EndAngle=4.71239
    g1: ArcOfCircle CenterX=-49.19 CenterY=62 CenterZ=0 NormalX=0 NormalY=0 NormalZ=1 AngleXU=0 Radius=1.5 StartAngle=1.5708 EndAngle=4.71239
    g2: ArcOfCircle CenterX=-49.19 CenterY=56.25 CenterZ=0 NormalX=0 NormalY=0 NormalZ=1 AngleXU=0 Radius=1.5 StartAngle=1.5708 EndAngle=4.71239
    g3: ArcOfCircle CenterX=-49.19 CenterY=50.5 CenterZ=0 NormalX=0 NormalY=0 NormalZ=1 AngleXU=0 Radius=1.5 StartAngle=1.5708 EndAngle=4.71239
    g4: ArcOfCircle CenterX=-49.19 CenterY=44.75 CenterZ=0 NormalX=0 NormalY=0 NormalZ=1 AngleXU=0 Radius=1.5 StartAngle=1.5708 EndAngle=4.71239
    g5: ArcOfCircle CenterX=-49.19 CenterY=39 CenterZ=0 NormalX=0 NormalY=0 NormalZ=1 AngleXU=0 Radius=1.5 StartAngle=1.5708 EndAngle=4.71239
    g6: ArcOfCircle CenterX=-49.19 CenterY=33 CenterZ=0 NormalX=0 NormalY=0 NormalZ=1 AngleXU=0 Radius=1.5 StartAngle=1.5708 EndAngle=4.71239
    g7: ArcOfCircle CenterX=-49.19 CenterY=27.25 CenterZ=0 NormalX=0 NormalY=0 NormalZ=1 AngleXU=0 Radius=1.5 StartAngle=1.5708 EndAngle=4.71239
    g8: ArcOfCircle CenterX=-49.19 CenterY=21.5 CenterZ=0 NormalX=0 NormalY=0 NormalZ=1 AngleXU=0 Radius=1.5 StartAngle=1.5708 EndAngle=4.71239
    g9: ArcOfCircle CenterX=-49.19 CenterY=15.75 CenterZ=0 NormalX=0 NormalY=0 NormalZ=1 AngleXU=0 Radius=1.5 StartAngle=1.5708 EndAngle=4.71239
    g10: ArcOfCircle CenterX=-49.19 CenterY=10 CenterZ=0 NormalX=0 NormalY=0 NormalZ=1 AngleXU=0 Radius=1.5 StartAngle=1.5708 EndAngle=4.71239
    g11: ArcOfCircle CenterX=-49.19 CenterY=4.25 CenterZ=0 NormalX=0 NormalY=0 NormalZ=1 AngleXU=0 Radius=1.5 StartAngle=1.5708 EndAngle=4.71239
    g12: LineSegment StartX=-49.19 StartY=69.25 StartZ=0 EndX=-49.19 EndY=66.25 EndZ=0
    g13: LineSegment StartX=-49.19 StartY=63.5 StartZ=0 EndX=-49.19 EndY=60.5 EndZ=0
    g14: LineSegment StartX=-49.19 StartY=57.75 StartZ=0 EndX=-49.19 EndY=54.75 EndZ=0
    g15: LineSegment StartX=-49.19 StartY=52 StartZ=0 EndX=-49.19 EndY=49 EndZ=0
    g16: LineSegment StartX=-49.19 StartY=46.25 StartZ=0 EndX=-49.19 EndY=43.25 EndZ=0
    g17: LineSegment StartX=-49.19 StartY=40.5 StartZ=0 EndX=-49.19 EndY=37.5 EndZ=0
    g18: LineSegment StartX=-49.19 StartY=34.5 StartZ=0 EndX=-49.19 EndY=31.5 EndZ=0
    g19: LineSegment StartX=-49.19 StartY=28.75 StartZ=0 EndX=-49.19 EndY=25.75 EndZ=0
    g20: LineSegment StartX=-49.19 StartY=23 StartZ=0 EndX=-49.19 EndY=20 EndZ=0
    g21: LineSegment StartX=-49.19 StartY=17.25 StartZ=0 EndX=-49.19 EndY=14.25 EndZ=0
    g22: LineSegment StartX=-49.19 StartY=11.5 StartZ=0 EndX=-49.19 EndY=8.5 EndZ=0
    g23: LineSegment StartX=-49.19 StartY=5.75 StartZ=0 EndX=-49.19 EndY=2.75 EndZ=0
  constraints (48):
    c: Block(g0)
    c: Block(g1)
    c: Block(g2)
    c: Block(g3)
    c: Block(g4)
    c: Block(g5)
    c: Block(g6)
    c: Block(g7)
    c: Block(g8)
    c: Block(g9)
    c: Block(g10)
    c: Block(g11)
    c: Coincident(g12,g0)
    c: Coincident(g12,g0)
    c: Vertical(g12)
    c: Vertical(g13)
    c: Coincident(g13,g1)
    c: Vertical(g14)
    c: Coincident(g14,g2)
    c: Vertical(g15)
    c: Coincident(g15,g3)
    c: Vertical(g16)
    c: Coincident(g16,g4)
    c: Vertical(g17)
    c: Coincident(g17,g5)
    c: Vertical(g18)
    c: Coincident(g18,g6)
    c: Vertical(g19)
    c: Coincident(g19,g7)
    c: Vertical(g20)
    c: Coincident(g20,g8)
    c: Vertical(g21)
    c: Coincident(g21,g9)
    c: Vertical(g22)
    c: Coincident(g22,g10)
    c: Vertical(g23)
    c: Coincident(g23,g11)
    c: Block(g23)
    c: Block(g22)
    c: Block(g21)
    c: Block(g20)
    c: Block(g13)
    c: Block(g14)
    c: Block(g15)
    c: Block(g16)
    c: Block(g17)
    c: Block(g18)
    c: Block(g19)
FEATURE [Part::Extrusion] Extrude022
  Base = -> Sketch030
  Dir = (1,-2e-16,2e-16)
  DirMode = 2
  FaceMakerClass = Part::FaceMakerBullseye
  LengthFwd = 19
  LengthRev = 0
  Placement = pos=(-19,0,0) rot=(0,0,1;0rad)
  Solid = true
  Symmetric = false
FEATURE [Part::Fillet] Fillet022
  Base = -> Extrude022
  Edges = 24 edges r=1.49: [Edge6,Edge11,Edge18,Edge23,Edge30,Edge35,Edge42,Edge47,Edge54,Edge59,Edge66,Edge71,Edge78,Edge83,Edge90,Edge95,Edge102,Edge107,Edge114,Edge119,Edge126,Edge131,Edge138,Edge143]
FEATURE [Part::Cut] Cut020  label="top010"
  Base = -> Cut019
  Tool = -> Fillet022
FEATURE [Sketcher::SketchObject] Sketch032
  FullyConstrained = true
  Placement = pos=(117,19,0) rot=(0.57735,0.57735,0.57735;2.0944rad)
  sketch-geometry (48):
    g0: LineSegment StartX=-49.19 StartY=69.25 StartZ=0 EndX=-49.19 EndY=66.25 EndZ=0
    g1: LineSegment StartX=-49.19 StartY=63.5 StartZ=0 EndX=-49.19 EndY=60.5 EndZ=0
    g2: LineSegment StartX=-49.19 StartY=57.75 StartZ=0 EndX=-49.19 EndY=54.75 EndZ=0
    g3: LineSegment StartX=-49.19 StartY=52 StartZ=0 EndX=-49.19 EndY=49 EndZ=0
    g4: LineSegment StartX=-49.19 StartY=46.25 StartZ=0 EndX=-49.19 EndY=43.25 EndZ=0
    g5: LineSegment StartX=-49.19 StartY=40.5 StartZ=0 EndX=-49.19 EndY=37.5 EndZ=0
    g6: LineSegment StartX=-49.19 StartY=34.5 StartZ=0 EndX=-49.19 EndY=31.5 EndZ=0
    g7: LineSegment StartX=-49.19 StartY=28.75 StartZ=0 EndX=-49.19 EndY=25.75 EndZ=0
    g8: LineSegment StartX=-49.19 StartY=23 StartZ=0 EndX=-49.19 EndY=20 EndZ=0
    g9: LineSegment StartX=-49.19 StartY=17.25 StartZ=0 EndX=-49.19 EndY=14.25 EndZ=0
    g10: LineSegment StartX=-49.19 StartY=11.5 StartZ=0 EndX=-49.19 EndY=8.5 EndZ=0
    g11: LineSegment StartX=-49.19 StartY=5.75 StartZ=0 EndX=-49.19 EndY=2.75 EndZ=0
    g12: ArcOfCircle CenterX=-1.5 CenterY=67.75 CenterZ=0 NormalX=0 NormalY=0 NormalZ=1 AngleXU=0 Radius=1.5 StartAngle=4.71239 EndAngle=7.85398
    g13: ArcOfCircle CenterX=-1.5 CenterY=62 CenterZ=0 NormalX=0 NormalY=0 NormalZ=1 AngleXU=0 Radius=1.5 StartAngle=4.71239 EndAngle=7.85398
    g14: ArcOfCircle CenterX=-1.5 CenterY=56.25 CenterZ=0 NormalX=0 NormalY=0 NormalZ=1 AngleXU=0 Radius=1.5 StartAngle=4.71239 EndAngle=7.85398
    g15: ArcOfCircle CenterX=-11.49 CenterY=50.5 CenterZ=0 NormalX=0 NormalY=0 NormalZ=1 AngleXU=0 Radius=1.5 StartAngle=4.71239 EndAngle=7.85398
    g16: ArcOfCircle CenterX=-16.28 CenterY=44.75 CenterZ=0 NormalX=0 NormalY=0 NormalZ=1 AngleXU=0 Radius=1.5 StartAngle=4.71239 EndAngle=7.85398
    g17: ArcOfCircle CenterX=-18.2337 CenterY=39 CenterZ=0 NormalX=0 NormalY=0 NormalZ=1 AngleXU=0 Radius=1.5 StartAngle=4.71485 EndAngle=7.85398
    g18: ArcOfCircle CenterX=-16.2837 CenterY=27.25 CenterZ=0 NormalX=0 NormalY=0 NormalZ=1 AngleXU=0 Radius=1.5 StartAngle=4.71485 EndAngle=7.85398
    g19: ArcOfCircle CenterX=-18.2337 CenterY=33 CenterZ=0 NormalX=0 NormalY=0 NormalZ=1 AngleXU=0 Radius=1.5 StartAngle=4.71485 EndAngle=7.85398
    g20: ArcOfCircle CenterX=-11.49 CenterY=21.5 CenterZ=0 NormalX=0 NormalY=0 NormalZ=1 AngleXU=0 Radius=1.5 StartAngle=4.71239 EndAngle=7.85398
    g21: ArcOfCircle CenterX=-1.5 CenterY=4.25 CenterZ=0 NormalX=0 NormalY=0 NormalZ=1 AngleXU=0 Radius=1.5 StartAngle=4.71239 EndAngle=7.85398
    g22: ArcOfCircle CenterX=-1.5 CenterY=10 CenterZ=0 NormalX=0 NormalY=0 NormalZ=1 AngleXU=0 Radius=1.5 StartAngle=4.71239 EndAngle=7.85398
    g23: ArcOfCircle CenterX=-1.5 CenterY=15.75 CenterZ=0 NormalX=0 NormalY=0 NormalZ=1 AngleXU=0 Radius=1.5 StartAngle=4.71239 EndAngle=7.85398
    g24: LineSegment StartX=-49.19 StartY=69.25 StartZ=0 EndX=-1.5 EndY=69.25 EndZ=0
    g25: LineSegment StartX=-49.19 StartY=66.25 StartZ=0 EndX=-1.5 EndY=66.25 EndZ=0
    g26: LineSegment StartX=-49.19 StartY=63.5 StartZ=0 EndX=-1.5 EndY=63.5 EndZ=0
    g27: LineSegment StartX=-49.19 StartY=60.5 StartZ=0 EndX=-1.5 EndY=60.5 EndZ=0
    g28: LineSegment StartX=-49.19 StartY=57.75 StartZ=0 EndX=-1.5 EndY=57.75 EndZ=0
    g29: LineSegment StartX=-49.19 StartY=54.75 StartZ=0 EndX=-1.5 EndY=54.75 EndZ=0
    g30: LineSegment StartX=-49.19 StartY=52 StartZ=0 EndX=-11.49 EndY=52 EndZ=0
    g31: LineSegment StartX=-49.19 StartY=49 StartZ=0 EndX=-11.49 EndY=49 EndZ=0
    g32: LineSegment StartX=-49.19 StartY=46.25 StartZ=0 EndX=-16.28 EndY=46.25 EndZ=0
    g33: LineSegment StartX=-49.19 StartY=43.25 StartZ=0 EndX=-16.28 EndY=43.25 EndZ=0
    g34: LineSegment StartX=-49.19 StartY=40.5 StartZ=0 EndX=-18.2337 EndY=40.5 EndZ=0
    g35: LineSegment StartX=-49.19 StartY=37.5 StartZ=0 EndX=-18.23 EndY=37.5 EndZ=0
    g36: LineSegment StartX=-49.19 StartY=34.5 StartZ=0 EndX=-18.2337 EndY=34.5 EndZ=0
    g37: LineSegment StartX=-49.19 StartY=31.5 StartZ=0 EndX=-18.23 EndY=31.5 EndZ=0
    g38: LineSegment StartX=-49.19 StartY=28.75 StartZ=0 EndX=-16.2837 EndY=28.75 EndZ=0
    g39: LineSegment StartX=-49.19 StartY=25.75 StartZ=0 EndX=-16.28 EndY=25.75 EndZ=0
    g40: LineSegment StartX=-49.19 StartY=23 StartZ=0 EndX=-11.49 EndY=23 EndZ=0
    g41: LineSegment StartX=-49.19 StartY=20 StartZ=0 EndX=-11.49 EndY=20 EndZ=0
    g42: LineSegment StartX=-49.19 StartY=17.25 StartZ=0 EndX=-1.5 EndY=17.25 EndZ=0
    g43: LineSegment StartX=-49.19 StartY=14.25 StartZ=0 EndX=-1.5 EndY=14.25 EndZ=0
    g44: LineSegment StartX=-49.19 StartY=11.5 StartZ=0 EndX=-1.5 EndY=11.5 EndZ=0
    g45: LineSegment StartX=-49.19 StartY=8.5 StartZ=0 EndX=-1.5 EndY=8.5 EndZ=0
    g46: LineSegment StartX=-49.19 StartY=5.75 StartZ=0 EndX=-1.5 EndY=5.75 EndZ=0
    g47: LineSegment StartX=-49.19 StartY=2.75 StartZ=0 EndX=-1.5 EndY=2.75 EndZ=0
  constraints (120):
    c: Vertical(g0)
    c: Distance(g0) = 3
    c: Block(g0)
    c: Vertical(g1)
    c: Distance(g1) = 3
    c: Vertical(g2)
    c: Equal(g0,g2) = 3
    c: Block(g2)
    c: Vertical(g3)
    c: Equal(g1,g3) = 3
    c: Vertical(g4)
    c: Equal(g0,g4) = 3
    c: Block(g4)
    c: Vertical(g5)
    c: Equal(g1,g5) = 3
    c: Vertical(g6)
    c: Equal(g0,g6) = 3
    c: Block(g6)
    c: Vertical(g7)
    c: Equal(g1,g7) = 3
    c: Vertical(g8)
    c: Equal(g0,g8) = 3
    c: Block(g8)
    c: Vertical(g9)
    c: Equal(g1,g9) = 3
    c: Vertical(g10)
    c: Equal(g0,g10) = 3
    c: Block(g10)
    c: Vertical(g11)
    c: Equal(g1,g11) = 3
    c: Block(g12)
    c: Block(g13)
    c: Block(g14)
    c: Block(g15)
    c: Block(g16)
    c: Block(g17)
    c: Block(g18)
    c: Block(g19)
    c: Block(g20)
    c: Block(g21)
    c: Block(g22)
    c: Block(g23)
    c: Block(g11)
    c: Block(g9)
    c: Block(g7)
    c: Block(g5)
    c: Block(g3)
    c: Block(g1)
    c: Coincident(g24,g0)
    c: Coincident(g24,g12)
    c: Horizontal(g24)
    c: Coincident(g25,g0)
    c: Coincident(g25,g12)
    c: Horizontal(g25)
    c: Coincident(g26,g1)
    c: Coincident(g26,g13)
    c: Horizontal(g26)
    c: Coincident(g27,g1)
    c: Coincident(g27,g13)
    c: Horizontal(g27)
    c: Coincident(g28,g2)
    c: Coincident(g28,g14)
    c: Horizontal(g28)
    c: Coincident(g29,g2)
    c: Coincident(g29,g14)
    c: Horizontal(g29)
    c: Coincident(g30,g3)
    c: Coincident(g30,g15)
    c: Horizontal(g30)
    c: Coincident(g31,g3)
    c: Coincident(g31,g15)
    c: Horizontal(g31)
    c: Coincident(g32,g4)
    c: Coincident(g32,g16)
    c: Horizontal(g32)
    c: Coincident(g33,g4)
    c: Coincident(g33,g16)
    c: Horizontal(g33)
    c: Coincident(g34,g5)
    c: Coincident(g34,g17)
    c: Horizontal(g34)
    c: Coincident(g35,g5)
    c: Coincident(g35,g17)
    c: Horizontal(g35)
    c: Coincident(g36,g6)
    c: Coincident(g36,g19)
    c: Horizontal(g36)
    c: Coincident(g37,g6)
    c: Coincident(g37,g19)
    c: Horizontal(g37)
    c: Coincident(g38,g7)
    c: Coincident(g38,g18)
    c: Horizontal(g38)
    c: Coincident(g39,g7)
    c: Coincident(g39,g18)
    c: Horizontal(g39)
    c: Coincident(g40,g8)
    c: Coincident(g40,g20)
    c: Horizontal(g40)
    c: Coincident(g41,g8)
    c: Coincident(g41,g20)
    c: Horizontal(g41)
    c: Coincident(g42,g9)
    c: Coincident(g42,g23)
    c: Horizontal(g42)
    c: Coincident(g43,g9)
    c: Coincident(g43,g23)
    c: Horizontal(g43)
    c: Coincident(g44,g10)
    c: Coincident(g44,g22)
    c: Horizontal(g44)
    c: Coincident(g45,g10)
    c: Coincident(g45,g22)
    c: Horizontal(g45)
    c: Coincident(g46,g11)
    c: Coincident(g46,g21)
    c: Horizontal(g46)
    c: Coincident(g47,g11)
    c: Coincident(g47,g21)
    c: Horizontal(g47)
FEATURE [Part::Extrusion] Extrude023
  Base = -> Sketch032
  Dir = (1,-2e-16,2e-16)
  DirMode = 2
  FaceMakerClass = Part::FaceMakerBullseye
  LengthFwd = 19
  LengthRev = 0
  Placement = pos=(-19,0,0) rot=(0,0,1;0rad)
  Solid = true
  Symmetric = false
FEATURE [Part::Fillet] Fillet023
  Base = -> Extrude023
  Edges = 24 edges r=1.49: [Edge6,Edge11,Edge18,Edge23,Edge30,Edge35,Edge42,Edge47,Edge54,Edge59,Edge66,Edge71,Edge78,Edge83,Edge90,Edge95,Edge102,Edge107,Edge114,Edge119,Edge126,Edge131,Edge138,Edge143]
  Placement = pos=(0,0.05,0) rot=(0,0,1;0rad)
FEATURE [Part::Cut] Cut014  label="bottom003"
  Base = -> Cut007
  Tool = -> Fusion047
FEATURE [Part::Cut] Cut021
  Base = -> Cut014
  Tool = -> Fillet023
FEATURE [Sketcher::SketchObject] Sketch033
  FullyConstrained = true
  Placement = pos=(117,19,0) rot=(0.57735,0.57735,0.57735;2.0944rad)
  sketch-geometry (8):
    g0: LineSegment StartX=-49.19 StartY=69.25 StartZ=0 EndX=-49.19 EndY=66.25 EndZ=0
    g1: LineSegment StartX=-49.19 StartY=5.75 StartZ=0 EndX=-49.19 EndY=2.75 EndZ=0
    g2: ArcOfCircle CenterX=-1.5 CenterY=67.75 CenterZ=0 NormalX=0 NormalY=0 NormalZ=1 AngleXU=0 Radius=1.5 StartAngle=4.71239 EndAngle=7.85398
    g3: ArcOfCircle CenterX=-1.5 CenterY=4.25 CenterZ=0 NormalX=0 NormalY=0 NormalZ=1 AngleXU=0 Radius=1.5 StartAngle=4.71239 EndAngle=7.85398
    g4: LineSegment StartX=-49.19 StartY=69.25 StartZ=0 EndX=-1.5 EndY=69.25 EndZ=0
    g5: LineSegment StartX=-49.19 StartY=66.25 StartZ=0 EndX=-1.5 EndY=66.25 EndZ=0
    g6: LineSegment StartX=-49.19 StartY=5.75 StartZ=0 EndX=-1.5 EndY=5.75 EndZ=0
    g7: LineSegment StartX=-49.19 StartY=2.75 StartZ=0 EndX=-1.5 EndY=2.75 EndZ=0
  constraints (19):
    c: Vertical(g0)
    c: Distance(g0) = 3
    c: Block(g0)
    c: Vertical(g1)
    c: Block(g2)
    c: Block(g3)
    c: Block(g1)
    c: Coincident(g4,g0)
    c: Coincident(g4,g2)
    c: Horizontal(g4)
    c: Coincident(g5,g0)
    c: Coincident(g5,g2)
    c: Horizontal(g5)
    c: Coincident(g6,g1)
    c: Coincident(g6,g3)
    c: Horizontal(g6)
    c: Coincident(g7,g1)
    c: Coincident(g7,g3)
    c: Horizontal(g7)
FEATURE [Sketcher::SketchObject] Sketch034
  FullyConstrained = true
  Placement = pos=(117,19,0) rot=(0.57735,0.57735,0.57735;2.0944rad)
  sketch-geometry (8):
    g0: LineSegment StartX=-49.19 StartY=63.5 StartZ=0 EndX=-49.19 EndY=60.5 EndZ=0
    g1: LineSegment StartX=-49.19 StartY=11.5 StartZ=0 EndX=-49.19 EndY=8.5 EndZ=0
    g2: ArcOfCircle CenterX=-1.5 CenterY=62 CenterZ=0 NormalX=0 NormalY=0 NormalZ=1 AngleXU=0 Radius=1.5 StartAngle=4.71239 EndAngle=7.85398
    g3: ArcOfCircle CenterX=-1.5 CenterY=10 CenterZ=0 NormalX=0 NormalY=0 NormalZ=1 AngleXU=0 Radius=1.5 StartAngle=4.71239 EndAngle=7.85398
    g4: LineSegment StartX=-49.19 StartY=63.5 StartZ=0 EndX=-1.5 EndY=63.5 EndZ=0
    g5: LineSegment StartX=-49.19 StartY=60.5 StartZ=0 EndX=-1.5 EndY=60.5 EndZ=0
    g6: LineSegment StartX=-49.19 StartY=11.5 StartZ=0 EndX=-1.5 EndY=11.5 EndZ=0
    g7: LineSegment StartX=-49.19 StartY=8.5 StartZ=0 EndX=-1.5 EndY=8.5 EndZ=0
  constraints (19):
    c: Vertical(g0)
    c: Distance(g0) = 3
    c: Vertical(g1)
    c: Block(g1)
    c: Block(g2)
    c: Block(g3)
    c: Block(g0)
    c: Coincident(g4,g0)
    c: Coincident(g4,g2)
    c: Horizontal(g4)
    c: Coincident(g5,g0)
    c: Coincident(g5,g2)
    c: Horizontal(g5)
    c: Coincident(g6,g1)
    c: Coincident(g6,g3)
    c: Horizontal(g6)
    c: Coincident(g7,g1)
    c: Coincident(g7,g3)
    c: Horizontal(g7)
FEATURE [Part::Extrusion] Extrude024
  Base = -> Sketch033
  Dir = (1,0,0)
  DirMode = 2
  FaceMakerClass = Part::FaceMakerBullseye
  LengthFwd = 10
  LengthRev = 0
  Solid = true
  Symmetric = false
FEATURE [Part::Extrusion] Extrude025
  Base = -> Sketch034
  Dir = (1,0,0)
  DirMode = 2
  FaceMakerClass = Part::FaceMakerBullseye
  LengthFwd = 10
  LengthRev = 0
  Solid = true
  Symmetric = false
FEATURE [Part::Fillet] Fillet024  label="removeFromtMoreFrontCaseScrewRetainers"
  Base = -> Extrude024
  Edges = 4 edges r=1.49: [Edge6,Edge11,Edge18,Edge23]
  Placement = pos=(-11,0,0) rot=(0,0,1;0rad)
FEATURE [Part::Fillet] Fillet025  label="removeFromtMoreFrontCaseScrewRetainers001"
  Base = -> Extrude025
  Edges = 4 edges r=1.49: [Edge6,Edge11,Edge18,Edge23]
  Placement = pos=(-19,0,0) rot=(0,0,1;0rad)
FEATURE [Part::Cut] Cut022
  Base = -> Cut015
  Tool = -> Fillet025
FEATURE [Part::Cut] Cut023
  Base = -> Cut022
  Tool = -> Fillet024
